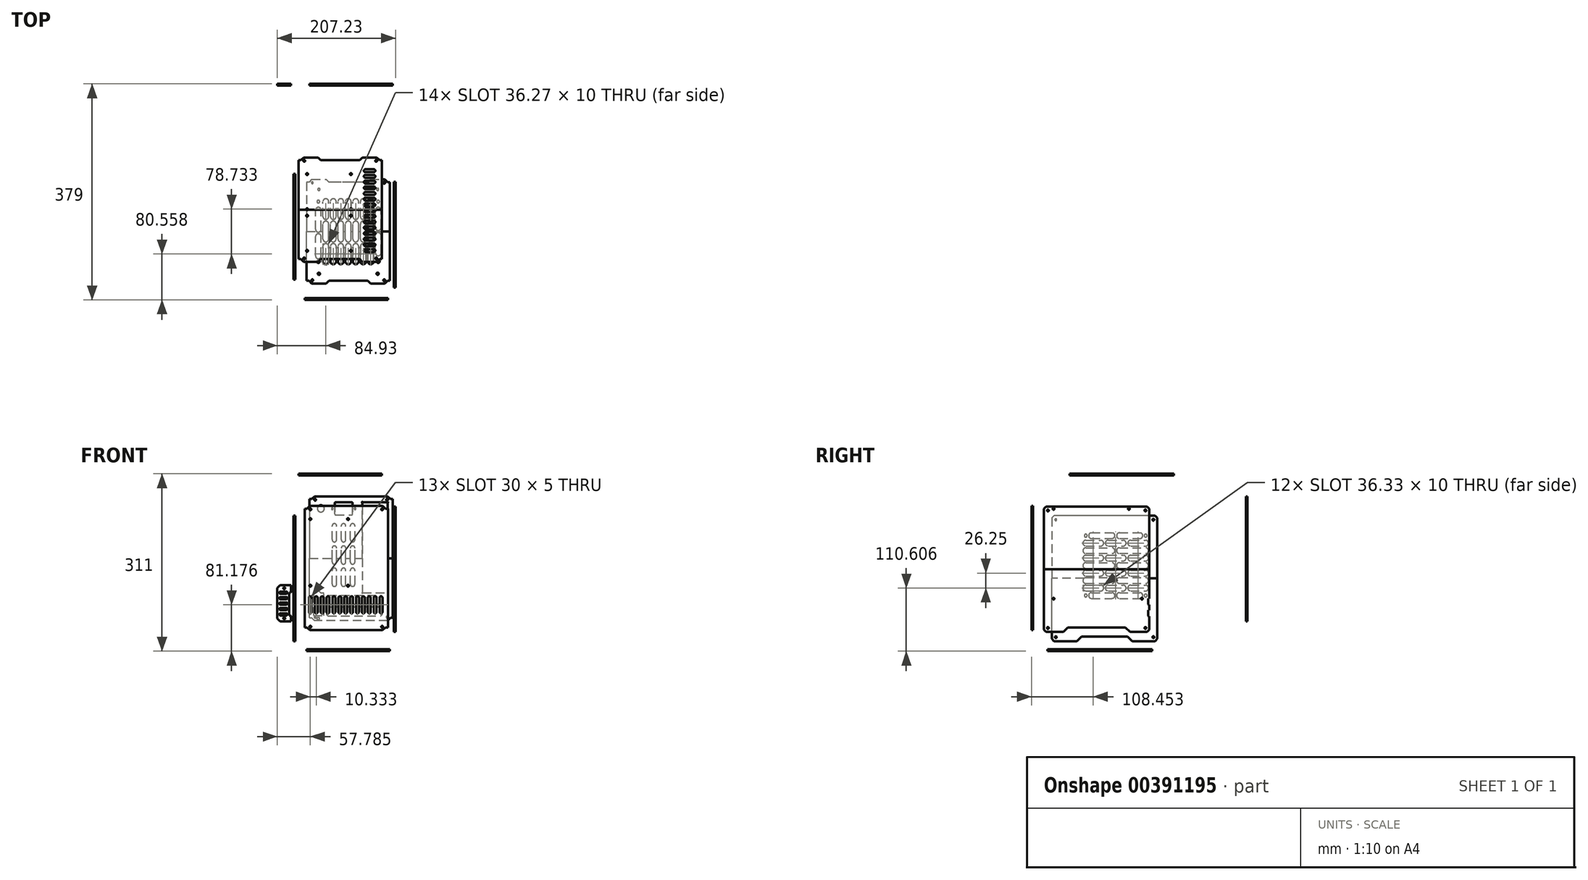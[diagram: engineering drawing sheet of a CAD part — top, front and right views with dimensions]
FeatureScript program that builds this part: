
annotation { "Feature Type Name" : "Feature", "Feature Type Description" : "" }
export const myFeature = defineFeature(function(context is Context, id is Id, definition is map)
    precondition{}
    {
        {
            var Q0;
            Q0=qCreatedBy(makeId("Front.planeOp"),FACE);
            var sketch = newSketch(context, id + "F0", { "sketchPlane" : qUnion([Q0])});
            skLineSegment(sketch, "E0.bottom", {"start": v(-76.44, 105.68) * mm, "end": v(69.56, 105.68) * mm});
            skLineSegment(sketch, "E0.top", {"start": v(-76.44, -7.32) * mm, "end": v(69.56, -7.32) * mm});
            skLineSegment(sketch, "E0.left", {"start": v(-76.44, 105.68) * mm, "end": v(-76.44, -7.32) * mm});
            skLineSegment(sketch, "E0.right", {"start": v(69.56, 105.68) * mm, "end": v(69.56, -7.32) * mm});
            skLineSegment(sketch, "E1", {"start": v(-76.44, 96.68) * mm, "end": v(-72.44, 96.68) * mm});
            skLineSegment(sketch, "E2", {"start": v(-72.44, 96.68) * mm, "end": v(-67.44, 101.68) * mm});
            skLineSegment(sketch, "E3", {"start": v(69.56, 96.68) * mm, "end": v(65.56, 96.68) * mm});
            skLineSegment(sketch, "E4", {"start": v(60.56, 101.68) * mm, "end": v(-67.44, 101.68) * mm});
            skLineSegment(sketch, "E5", {"start": v(60.56, 101.68) * mm, "end": v(65.56, 96.68) * mm});
            skLineSegment(sketch, "E6", {"start": v(-76.44, 95.68) * mm, "end": v(-66.44, 95.68) * mm, "construction": true});
            skCircle(sketch, "E7", {"center": v(-66.44, 95.68) * mm, "radius": 1.6 * mm});
            skLineSegment(sketch, "E8", {"start": v(69.56, 95.68) * mm, "end": v(59.56, 95.68) * mm, "construction": true});
            skCircle(sketch, "E9", {"center": v(59.56, 95.68) * mm, "radius": 1.6 * mm});
            skSolve(sketch);
        }
        {
            var Q0;
            {var subQ1=sQuery(id+"F0.wireOp",EDGE,"E0.top");Q0=makeQuery(id+"F0.imprint","IMPRINT",FACE,{"disambiguationData":[TD([[makeQuery(id+"F0.imprint","IMPRINT",EDGE,{"derivedFrom":subQ1}),1.0]])]});}
            extrude(context, id + "F1", {"entities" : qUnion([Q0]), "depth" : 3 * mm});
        }
        {
            var Q0;
            Q0=makeQuery(id+"F1.opExtrude","SWEPT_BODY",BODY,{"disambiguationData":[OSD([sQuery(id+"F0.wireOp",EDGE,"E0.bottom"),sQuery(id+"F0.wireOp",EDGE,"E0.top"),sQuery(id+"F0.wireOp",EDGE,"E0.left"),sQuery(id+"F0.wireOp",EDGE,"E0.right"),sQuery(id+"F0.wireOp",EDGE,"E1"),sQuery(id+"F0.wireOp",EDGE,"E2"),sQuery(id+"F0.wireOp",EDGE,"8kIEKiAh-QTEb-dtpp-JcTS-wpPMPQfBbqQd"),sQuery(id+"F0.wireOp",EDGE,"IAD0FTGy-GJaP-wMLm-guci-XfnhwucHu2uu"),sQuery(id+"F0.wireOp",EDGE,"IvHsRxJE-VIxi-RXbs-pRJC-tqeUj7lQNFDg"),sQuery(id+"F0.wireOp",EDGE,"jDx6nEBO-jJHg-Gf5S-wIms-nsZNRVFYcTxt")])]});
            var Q1;
            Q1=makeQuery(id+"F1.opExtrude","SWEPT_FACE",FACE,{"disambiguationData":[OSD([sQuery(id+"F0.wireOp",EDGE,"E0.top")])]});
            mirror(context, id + "F2", {"operationType" : NewBodyOperationType.ADD, "entities" : qUnion([Q0]), "mirrorPlane" : qUnion([Q1])});
        }
        {
            var Q0;
            {var subQ0=makeQuery(id+"F1.opExtrude","CAP_FACE",FACE,{"disambiguationData":[OSD([sQuery(id+"F0.wireOp",EDGE,"E0.bottom"),sQuery(id+"F0.wireOp",EDGE,"E0.top"),sQuery(id+"F0.wireOp",EDGE,"E0.left"),sQuery(id+"F0.wireOp",EDGE,"E0.right"),sQuery(id+"F0.wireOp",EDGE,"E1"),sQuery(id+"F0.wireOp",EDGE,"E2"),sQuery(id+"F0.wireOp",EDGE,"8kIEKiAh-QTEb-dtpp-JcTS-wpPMPQfBbqQd"),sQuery(id+"F0.wireOp",EDGE,"IAD0FTGy-GJaP-wMLm-guci-XfnhwucHu2uu"),sQuery(id+"F0.wireOp",EDGE,"IvHsRxJE-VIxi-RXbs-pRJC-tqeUj7lQNFDg"),sQuery(id+"F0.wireOp",EDGE,"jDx6nEBO-jJHg-Gf5S-wIms-nsZNRVFYcTxt")])],"isStart":false});Q0=makeQuery(id+"F2.boolean.opBoolean","MERGE",FACE,{"derivedFrom":[subQ0,makeQuery(id+"F2.opPattern","COPY",FACE,{"derivedFrom":subQ0,"instanceName":"1"})]});}
            var sketch = newSketch(context, id + "F3", { "sketchPlane" : qUnion([Q0])});
            skLineSegment(sketch, "E10", {"start": v(-66.44, -84.32) * mm, "end": v(-66.44, -116.32) * mm, "construction": true});
            skLineSegment(sketch, "E11.bottom", {"start": v(-66.44, 78.68) * mm, "end": v(-0.24, 78.68) * mm, "construction": true});
            skLineSegment(sketch, "E11.top", {"start": v(-66.44, -38.32) * mm, "end": v(-0.24, -38.32) * mm, "construction": true});
            skLineSegment(sketch, "E11.left", {"start": v(-66.44, 78.68) * mm, "end": v(-66.44, -38.32) * mm, "construction": true});
            skLineSegment(sketch, "E11.right", {"start": v(-0.24, 78.68) * mm, "end": v(-0.24, -38.32) * mm, "construction": true});
            skLineSegment(sketch, "E12", {"start": v(-66.44, 78.68) * mm, "end": v(-76.44, 78.68) * mm, "construction": true});
            skCircle(sketch, "E13", {"center": v(-0.24, 78.68) * mm, "radius": 1.6 * mm});
            skCircle(sketch, "E14", {"center": v(-66.44, 78.68) * mm, "radius": 1.6 * mm});
            skCircle(sketch, "E15", {"center": v(-66.44, -38.32) * mm, "radius": 1.6 * mm});
            skCircle(sketch, "E16", {"center": v(-0.24, -38.32) * mm, "radius": 1.6 * mm});
            skLineSegment(sketch, "E17", {"start": v(-66.44, -84.32) * mm, "end": v(-66.44, -59.32) * mm, "construction": true});
            skArc(sketch, "E18.0.startCap", {"start": v(-63.94, -84.32) * mm, "mid": v(-66.44, -86.82) * mm, "end": v(-68.94, -84.32) * mm});
            skArc(sketch, "E18.0.endCap", {"start": v(-68.94, -59.32) * mm, "mid": v(-66.44, -56.82) * mm, "end": v(-63.94, -59.32) * mm});
            skLineSegment(sketch, "E18.0.left", {"start": v(-68.94, -84.32) * mm, "end": v(-68.94, -59.32) * mm});
            skLineSegment(sketch, "E18.0.right", {"start": v(-63.94, -84.32) * mm, "end": v(-63.94, -59.32) * mm});
            skLineSegment(sketch, "E19.1.0.0", {"start": v(-56.11, -84.32) * mm, "end": v(-56.11, -59.32) * mm, "construction": true});
            skArc(sketch, "E19.1.0.1", {"start": v(-53.61, -84.32) * mm, "mid": v(-56.11, -86.82) * mm, "end": v(-58.61, -84.32) * mm});
            skArc(sketch, "E19.1.0.2", {"start": v(-58.61, -59.32) * mm, "mid": v(-56.11, -56.82) * mm, "end": v(-53.61, -59.32) * mm});
            skLineSegment(sketch, "E19.1.0.3", {"start": v(-53.61, -84.32) * mm, "end": v(-53.61, -59.32) * mm});
            skLineSegment(sketch, "E19.1.0.4", {"start": v(-58.61, -84.32) * mm, "end": v(-58.61, -59.32) * mm});
            skLineSegment(sketch, "E19.2.0.0", {"start": v(-45.78, -84.32) * mm, "end": v(-45.78, -59.32) * mm, "construction": true});
            skArc(sketch, "E19.2.0.1", {"start": v(-43.28, -84.32) * mm, "mid": v(-45.78, -86.82) * mm, "end": v(-48.28, -84.32) * mm});
            skArc(sketch, "E19.2.0.2", {"start": v(-48.28, -59.32) * mm, "mid": v(-45.78, -56.82) * mm, "end": v(-43.28, -59.32) * mm});
            skLineSegment(sketch, "E19.2.0.3", {"start": v(-43.28, -84.32) * mm, "end": v(-43.28, -59.32) * mm});
            skLineSegment(sketch, "E19.2.0.4", {"start": v(-48.28, -84.32) * mm, "end": v(-48.28, -59.32) * mm});
            skLineSegment(sketch, "E19.3.0.0", {"start": v(-35.45, -84.32) * mm, "end": v(-35.45, -59.32) * mm, "construction": true});
            skArc(sketch, "E19.3.0.1", {"start": v(-32.95, -84.32) * mm, "mid": v(-35.45, -86.82) * mm, "end": v(-37.95, -84.32) * mm});
            skArc(sketch, "E19.3.0.2", {"start": v(-37.95, -59.32) * mm, "mid": v(-35.45, -56.82) * mm, "end": v(-32.95, -59.32) * mm});
            skLineSegment(sketch, "E19.3.0.3", {"start": v(-32.95, -84.32) * mm, "end": v(-32.95, -59.32) * mm});
            skLineSegment(sketch, "E19.3.0.4", {"start": v(-37.95, -84.32) * mm, "end": v(-37.95, -59.32) * mm});
            skLineSegment(sketch, "E19.4.0.0", {"start": v(-25.11, -84.32) * mm, "end": v(-25.11, -59.32) * mm, "construction": true});
            skArc(sketch, "E19.4.0.1", {"start": v(-22.61, -84.32) * mm, "mid": v(-25.11, -86.82) * mm, "end": v(-27.61, -84.32) * mm});
            skArc(sketch, "E19.4.0.2", {"start": v(-27.61, -59.32) * mm, "mid": v(-25.11, -56.82) * mm, "end": v(-22.61, -59.32) * mm});
            skLineSegment(sketch, "E19.4.0.3", {"start": v(-22.61, -84.32) * mm, "end": v(-22.61, -59.32) * mm});
            skLineSegment(sketch, "E19.4.0.4", {"start": v(-27.61, -84.32) * mm, "end": v(-27.61, -59.32) * mm});
            skLineSegment(sketch, "E19.5.0.0", {"start": v(-14.78, -84.32) * mm, "end": v(-14.78, -59.32) * mm, "construction": true});
            skArc(sketch, "E19.5.0.1", {"start": v(-12.28, -84.32) * mm, "mid": v(-14.78, -86.82) * mm, "end": v(-17.28, -84.32) * mm});
            skArc(sketch, "E19.5.0.2", {"start": v(-17.28, -59.32) * mm, "mid": v(-14.78, -56.82) * mm, "end": v(-12.28, -59.32) * mm});
            skLineSegment(sketch, "E19.5.0.3", {"start": v(-12.28, -84.32) * mm, "end": v(-12.28, -59.32) * mm});
            skLineSegment(sketch, "E19.5.0.4", {"start": v(-17.28, -84.32) * mm, "end": v(-17.28, -59.32) * mm});
            skLineSegment(sketch, "E19.6.0.0", {"start": v(-4.45, -84.32) * mm, "end": v(-4.45, -59.32) * mm, "construction": true});
            skArc(sketch, "E19.6.0.1", {"start": v(-1.95, -84.32) * mm, "mid": v(-4.45, -86.82) * mm, "end": v(-6.95, -84.32) * mm});
            skArc(sketch, "E19.6.0.2", {"start": v(-6.95, -59.32) * mm, "mid": v(-4.45, -56.82) * mm, "end": v(-1.95, -59.32) * mm});
            skLineSegment(sketch, "E19.6.0.3", {"start": v(-1.95, -84.32) * mm, "end": v(-1.95, -59.32) * mm});
            skLineSegment(sketch, "E19.6.0.4", {"start": v(-6.95, -84.32) * mm, "end": v(-6.95, -59.32) * mm});
            skLineSegment(sketch, "E19.7.0.0", {"start": v(5.89, -84.32) * mm, "end": v(5.89, -59.32) * mm, "construction": true});
            skArc(sketch, "E19.7.0.1", {"start": v(8.39, -84.32) * mm, "mid": v(5.89, -86.82) * mm, "end": v(3.39, -84.32) * mm});
            skArc(sketch, "E19.7.0.2", {"start": v(3.39, -59.32) * mm, "mid": v(5.89, -56.82) * mm, "end": v(8.39, -59.32) * mm});
            skLineSegment(sketch, "E19.7.0.3", {"start": v(8.39, -84.32) * mm, "end": v(8.39, -59.32) * mm});
            skLineSegment(sketch, "E19.7.0.4", {"start": v(3.39, -84.32) * mm, "end": v(3.39, -59.32) * mm});
            skLineSegment(sketch, "E19.8.0.0", {"start": v(16.22, -84.32) * mm, "end": v(16.22, -59.32) * mm, "construction": true});
            skArc(sketch, "E19.8.0.1", {"start": v(18.72, -84.32) * mm, "mid": v(16.22, -86.82) * mm, "end": v(13.72, -84.32) * mm});
            skArc(sketch, "E19.8.0.2", {"start": v(13.72, -59.32) * mm, "mid": v(16.22, -56.82) * mm, "end": v(18.72, -59.32) * mm});
            skLineSegment(sketch, "E19.8.0.3", {"start": v(18.72, -84.32) * mm, "end": v(18.72, -59.32) * mm});
            skLineSegment(sketch, "E19.8.0.4", {"start": v(13.72, -84.32) * mm, "end": v(13.72, -59.32) * mm});
            skLineSegment(sketch, "E19.9.0.0", {"start": v(26.55, -84.32) * mm, "end": v(26.55, -59.32) * mm, "construction": true});
            skArc(sketch, "E19.9.0.1", {"start": v(29.05, -84.32) * mm, "mid": v(26.55, -86.82) * mm, "end": v(24.05, -84.32) * mm});
            skArc(sketch, "E19.9.0.2", {"start": v(24.05, -59.32) * mm, "mid": v(26.55, -56.82) * mm, "end": v(29.05, -59.32) * mm});
            skLineSegment(sketch, "E19.9.0.3", {"start": v(29.05, -84.32) * mm, "end": v(29.05, -59.32) * mm});
            skLineSegment(sketch, "E19.9.0.4", {"start": v(24.05, -84.32) * mm, "end": v(24.05, -59.32) * mm});
            skLineSegment(sketch, "E19.10.0.0", {"start": v(36.89, -84.32) * mm, "end": v(36.89, -59.32) * mm, "construction": true});
            skArc(sketch, "E19.10.0.1", {"start": v(39.39, -84.32) * mm, "mid": v(36.89, -86.82) * mm, "end": v(34.39, -84.32) * mm});
            skArc(sketch, "E19.10.0.2", {"start": v(34.39, -59.32) * mm, "mid": v(36.89, -56.82) * mm, "end": v(39.39, -59.32) * mm});
            skLineSegment(sketch, "E19.10.0.3", {"start": v(39.39, -84.32) * mm, "end": v(39.39, -59.32) * mm});
            skLineSegment(sketch, "E19.10.0.4", {"start": v(34.39, -84.32) * mm, "end": v(34.39, -59.32) * mm});
            skLineSegment(sketch, "E19.11.0.0", {"start": v(47.22, -84.32) * mm, "end": v(47.22, -59.32) * mm, "construction": true});
            skArc(sketch, "E19.11.0.1", {"start": v(49.72, -84.32) * mm, "mid": v(47.22, -86.82) * mm, "end": v(44.72, -84.32) * mm});
            skArc(sketch, "E19.11.0.2", {"start": v(44.72, -59.32) * mm, "mid": v(47.22, -56.82) * mm, "end": v(49.72, -59.32) * mm});
            skLineSegment(sketch, "E19.11.0.3", {"start": v(49.72, -84.32) * mm, "end": v(49.72, -59.32) * mm});
            skLineSegment(sketch, "E19.11.0.4", {"start": v(44.72, -84.32) * mm, "end": v(44.72, -59.32) * mm});
            skLineSegment(sketch, "E19.12.0.0", {"start": v(57.55, -84.32) * mm, "end": v(57.55, -59.32) * mm, "construction": true});
            skArc(sketch, "E19.12.0.1", {"start": v(60.05, -84.32) * mm, "mid": v(57.55, -86.82) * mm, "end": v(55.05, -84.32) * mm});
            skArc(sketch, "E19.12.0.2", {"start": v(55.05, -59.32) * mm, "mid": v(57.55, -56.82) * mm, "end": v(60.05, -59.32) * mm});
            skLineSegment(sketch, "E19.12.0.3", {"start": v(60.05, -84.32) * mm, "end": v(60.05, -59.32) * mm});
            skLineSegment(sketch, "E19.12.0.4", {"start": v(55.05, -84.32) * mm, "end": v(55.05, -59.32) * mm});
            skLineSegment(sketch, "E19.direction1", {"start": v(-68.94, -84.32) * mm, "end": v(-58.61, -84.32) * mm, "construction": true});
            skSolve(sketch);
        }
        {
            var Q0;
            Q0=qSketchRegion(id+"F3",true);
            extrude(context, id + "F4", {"entities" : qUnion([Q0]), "operationType" : NewBodyOperationType.REMOVE, "oppositeDirection" : true, "depth" : 3 * mm});
        }
        {
            var Q0;
            Q0=qCreatedBy(makeId("Right.planeOp"),FACE);
            cPlane(context, id + "F5", {"entities" : qUnion([Q0]), "cplaneType" : CPlaneType.OFFSET, "offset" : 80 * mm, "width" : 150 * mm, "height" : 150 * mm});
        }
        {
            var Q0;
            Q0=qCreatedBy(id+"F5.planeOp",FACE);
            var sketch = newSketch(context, id + "F6", { "sketchPlane" : qUnion([Q0])});
            skLineSegment(sketch, "E20.bottom", {"start": v(18.91, 100.63) * mm, "end": v(203.91, 100.63) * mm});
            skLineSegment(sketch, "E20.top", {"start": v(18.91, -9.37) * mm, "end": v(203.91, -9.37) * mm});
            skLineSegment(sketch, "E20.left", {"start": v(18.91, 100.63) * mm, "end": v(18.91, -9.37) * mm});
            skLineSegment(sketch, "E20.right", {"start": v(203.91, 100.63) * mm, "end": v(203.91, -9.37) * mm});
            skLineSegment(sketch, "E21", {"start": v(18.91, 96.63) * mm, "end": v(22.91, 100.63) * mm});
            skLineSegment(sketch, "E22", {"start": v(199.91, 100.63) * mm, "end": v(203.91, 96.63) * mm});
            skLineSegment(sketch, "E23", {"start": v(18.91, 93.63) * mm, "end": v(25.91, 93.63) * mm, "construction": true});
            skCircle(sketch, "E24", {"center": v(25.91, 93.63) * mm, "radius": 1.6 * mm});
            skLineSegment(sketch, "E25", {"start": v(203.91, 93.63) * mm, "end": v(196.91, 93.63) * mm, "construction": true});
            skCircle(sketch, "E26", {"center": v(196.91, 93.63) * mm, "radius": 1.6 * mm});
            skSolve(sketch);
        }
        {
            var Q0;
            {var subQ4=sQuery(id+"F6.wireOp",EDGE,"E20.top");Q0=makeQuery(id+"F6.imprint","IMPRINT",FACE,{"disambiguationData":[TD([[makeQuery(id+"F6.imprint","IMPRINT",EDGE,{"derivedFrom":subQ4}),1.0]])]});}
            extrude(context, id + "F7", {"entities" : qUnion([Q0]), "depth" : 3 * mm});
        }
        {
            var Q0;
            Q0=makeQuery(id+"F7.opExtrude","SWEPT_BODY",BODY,{"disambiguationData":[OSD([sQuery(id+"F6.wireOp",EDGE,"E20.bottom"),sQuery(id+"F6.wireOp",EDGE,"E20.top"),sQuery(id+"F6.wireOp",EDGE,"E20.left"),sQuery(id+"F6.wireOp",EDGE,"E20.right"),sQuery(id+"F6.wireOp",EDGE,"uhohLnhp-hqEh-HnCf-sw5P-UAyFwgDYjcBT"),sQuery(id+"F6.wireOp",EDGE,"PZ9vbapj-Vyhe-IVd5-wSIB-ihSb0FTefDFo"),sQuery(id+"F6.wireOp",EDGE,"Vy2RlQAS-aQ6k-OJzX-lqoE-WAFZ4NoHzz8E"),sQuery(id+"F6.wireOp",EDGE,"uOpGianr-bHoC-LPpd-ZrnQ-WT6fRq75YZDk"),sQuery(id+"F6.wireOp",EDGE,"ByD4MoDk-9vtG-w2Bj-nV2I-deXss6nWGu8L"),sQuery(id+"F6.wireOp",EDGE,"dErzSW6J-HGX5-GNXE-lozc-OmhnMsFbACEc"),sQuery(id+"F6.wireOp",EDGE,"oiYVu7ST-duG0-g5FE-uATR-zlAqLM0uh895"),sQuery(id+"F6.wireOp",EDGE,"fhnCciFL-T4Vn-rBCZ-nkKt-uSig2OXv9zq8")])]});
            var Q1;
            Q1=makeQuery(id+"F7.opExtrude","SWEPT_FACE",FACE,{"disambiguationData":[OSD([sQuery(id+"F6.wireOp",EDGE,"E20.top")])]});
            mirror(context, id + "F8", {"operationType" : NewBodyOperationType.ADD, "entities" : qUnion([Q0]), "mirrorPlane" : qUnion([Q1])});
        }
        {
            var Q0;
            {var subQ0=makeQuery(id+"F7.opExtrude","CAP_FACE",FACE,{"disambiguationData":[OSD([sQuery(id+"F6.wireOp",EDGE,"E20.bottom"),sQuery(id+"F6.wireOp",EDGE,"E20.top"),sQuery(id+"F6.wireOp",EDGE,"E20.left"),sQuery(id+"F6.wireOp",EDGE,"E20.right"),sQuery(id+"F6.wireOp",EDGE,"E21"),sQuery(id+"F6.wireOp",EDGE,"E22")])],"isStart":true});Q0=makeQuery(id+"F8.boolean.opBoolean","MERGE",FACE,{"derivedFrom":[subQ0,makeQuery(id+"F8.opPattern","COPY",FACE,{"derivedFrom":subQ0,"instanceName":"1"})]});}
            var sketch = newSketch(context, id + "F9", { "sketchPlane" : qUnion([Q0])});
            skLineSegment(sketch, "E27", {"start": v(-200.91, -67.37) * mm, "end": v(-200.91, 102.63) * mm, "construction": true});
            skLineSegment(sketch, "E28", {"start": v(-200.91, -67.37) * mm, "end": v(-30.91, -67.37) * mm, "construction": true});
            skLineSegment(sketch, "E29", {"start": v(-200.91, 102.63) * mm, "end": v(-30.91, 102.63) * mm, "construction": true});
            skLineSegment(sketch, "E30", {"start": v(-30.91, 102.63) * mm, "end": v(-30.91, -67.37) * mm, "construction": true});
            skLineSegment(sketch, "E31", {"start": v(-200.91, -60.97) * mm, "end": v(-190.71, -60.97) * mm, "construction": true});
            skCircle(sketch, "E32", {"center": v(-190.71, -60.97) * mm, "radius": 1.5 * mm});
            skLineSegment(sketch, "E33", {"start": v(-190.71, -60.97) * mm, "end": v(-35.81, -60.97) * mm, "construction": true});
            skCircle(sketch, "E34", {"center": v(-35.81, -60.97) * mm, "radius": 1.5 * mm});
            skLineSegment(sketch, "E35", {"start": v(-200.91, 96.43) * mm, "end": v(-167.91, 96.43) * mm, "construction": true});
            skCircle(sketch, "E36", {"center": v(-167.91, 96.43) * mm, "radius": 1.5 * mm});
            skLineSegment(sketch, "E37", {"start": v(-167.91, 96.43) * mm, "end": v(-35.81, 96.43) * mm, "construction": true});
            skCircle(sketch, "E38", {"center": v(-35.81, 96.43) * mm, "radius": 1.5 * mm});
            skLineSegment(sketch, "E39", {"start": v(-52.91, -119.37) * mm, "end": v(-60.91, -111.37) * mm});
            skLineSegment(sketch, "E40", {"start": v(-60.91, -111.37) * mm, "end": v(-161.91, -111.37) * mm});
            skLineSegment(sketch, "E41", {"start": v(-161.91, -111.37) * mm, "end": v(-169.91, -119.37) * mm});
            skLineSegment(sketch, "E42", {"start": v(-52.91, -119.37) * mm, "end": v(-169.91, -119.37) * mm});
            skLineSegment(sketch, "E43.bottom", {"start": v(-201.91, -60.57) * mm, "end": v(-203.91, -60.57) * mm});
            skLineSegment(sketch, "E43.top", {"start": v(-201.91, -71.57) * mm, "end": v(-203.91, -71.57) * mm});
            skLineSegment(sketch, "E43.left", {"start": v(-201.91, -60.57) * mm, "end": v(-201.91, -71.57) * mm});
            skLineSegment(sketch, "E43.right", {"start": v(-203.91, -60.57) * mm, "end": v(-203.91, -71.57) * mm});
            skLineSegment(sketch, "E44", {"start": v(-201.91, -66.07) * mm, "end": v(-200.91, -66.07) * mm, "construction": true});
            skLineSegment(sketch, "E45.bottom", {"start": v(-201.91, -80.87) * mm, "end": v(-203.91, -80.87) * mm});
            skLineSegment(sketch, "E45.top", {"start": v(-201.91, -91.87) * mm, "end": v(-203.91, -91.87) * mm});
            skLineSegment(sketch, "E45.left", {"start": v(-201.91, -80.87) * mm, "end": v(-201.91, -91.87) * mm});
            skLineSegment(sketch, "E45.right", {"start": v(-203.91, -80.87) * mm, "end": v(-203.91, -91.87) * mm});
            skLineSegment(sketch, "E46", {"start": v(-203.91, -80.87) * mm, "end": v(-203.91, -71.57) * mm, "construction": true});
            skLineSegment(sketch, "E47", {"start": v(-201.91, -71.57) * mm, "end": v(-201.91, -80.87) * mm, "construction": true});
            skLineSegment(sketch, "E48", {"start": v(-203.91, -86.37) * mm, "end": v(-207.88, -86.37) * mm, "construction": true});
            skLineSegment(sketch, "E49", {"start": v(-207.88, -86.37) * mm, "end": v(-207.88, -66.07) * mm, "construction": true});
            skPoint(sketch, "E49.endSnap0", {"position": v(-203.91, -66.07) * mm});
            skLineSegment(sketch, "E50", {"start": v(-207.88, -66.07) * mm, "end": v(-203.91, -66.07) * mm, "construction": true});
            skSolve(sketch);
        }
        {
            var Q0;
            Q0=qSketchRegion(id+"F9",true);
            var Q1;
            {var subQ0=sQuery(id+"F9.wireOp",EDGE,"b6TVsvgF-kPWZ-6Ni7-LZi2-MRGtpnM4VBQ9");Q1=makeQuery(id+"F9.imprint","IMPRINT",FACE,{"disambiguationData":[TD([[makeQuery(id+"F9.imprint","IMPRINT",EDGE,{"derivedFrom":subQ0}),-1.0]])]});}
            extrude(context, id + "F10", {"entities" : qUnion([Q0, Q1]), "operationType" : NewBodyOperationType.REMOVE, "oppositeDirection" : true, "depth" : 25 * mm});
        }
        {
            var Q0;
            Q0=qCreatedBy(makeId("Right.planeOp"),FACE);
            cPlane(context, id + "F11", {"entities" : qUnion([Q0]), "cplaneType" : CPlaneType.OFFSET, "offset" : 96 * mm, "oppositeDirection" : true, "width" : 150 * mm, "height" : 150 * mm});
        }
        {
            var Q0;
            Q0=qCreatedBy(id+"F11.planeOp",FACE);
            var sketch = newSketch(context, id + "F12", { "sketchPlane" : qUnion([Q0])});
            skLineSegment(sketch, "E51.bottom", {"start": v(217.79, 84.48) * mm, "end": v(32.79, 84.48) * mm});
            skLineSegment(sketch, "E51.top", {"start": v(217.79, -25.52) * mm, "end": v(32.79, -25.52) * mm});
            skLineSegment(sketch, "E51.left", {"start": v(217.79, 84.48) * mm, "end": v(217.79, -25.52) * mm});
            skLineSegment(sketch, "E51.right", {"start": v(32.79, 84.48) * mm, "end": v(32.79, -25.52) * mm});
            skLineSegment(sketch, "E52", {"start": v(217.79, 80.48) * mm, "end": v(213.79, 84.48) * mm});
            skLineSegment(sketch, "E53", {"start": v(36.79, 84.48) * mm, "end": v(32.79, 80.48) * mm});
            skLineSegment(sketch, "E54", {"start": v(217.79, 77.48) * mm, "end": v(210.79, 77.48) * mm, "construction": true});
            skCircle(sketch, "E55", {"center": v(210.79, 77.48) * mm, "radius": 1.6 * mm});
            skLineSegment(sketch, "E56", {"start": v(32.79, 77.48) * mm, "end": v(39.79, 77.48) * mm, "construction": true});
            skCircle(sketch, "E57", {"center": v(39.79, 77.48) * mm, "radius": 1.6 * mm});
            skSolve(sketch);
        }
        {
            var Q0;
            {var subQ1=sQuery(id+"F12.wireOp",EDGE,"E51.top");Q0=makeQuery(id+"F12.imprint","IMPRINT",FACE,{"disambiguationData":[TD([[makeQuery(id+"F12.imprint","IMPRINT",EDGE,{"derivedFrom":subQ1}),-1.0]])]});}
            extrude(context, id + "F13", {"entities" : qUnion([Q0]), "depth" : 3 * mm});
        }
        {
            var Q0;
            Q0=makeQuery(id+"F13.opExtrude","SWEPT_BODY",BODY,{"disambiguationData":[OSD([sQuery(id+"F12.wireOp",EDGE,"E51.bottom"),sQuery(id+"F12.wireOp",EDGE,"E51.top"),sQuery(id+"F12.wireOp",EDGE,"E51.left"),sQuery(id+"F12.wireOp",EDGE,"E51.right"),sQuery(id+"F12.wireOp",EDGE,"E52"),sQuery(id+"F12.wireOp",EDGE,"E53")])]});
            var Q1;
            Q1=makeQuery(id+"F13.opExtrude","SWEPT_FACE",FACE,{"disambiguationData":[OSD([sQuery(id+"F12.wireOp",EDGE,"E51.top")])]});
            mirror(context, id + "F14", {"operationType" : NewBodyOperationType.ADD, "entities" : qUnion([Q0]), "mirrorPlane" : qUnion([Q1])});
        }
        {
            var Q0;
            {var subQ0=makeQuery(id+"F13.opExtrude","CAP_FACE",FACE,{"disambiguationData":[OSD([sQuery(id+"F12.wireOp",EDGE,"E51.bottom"),sQuery(id+"F12.wireOp",EDGE,"E51.top"),sQuery(id+"F12.wireOp",EDGE,"E51.left"),sQuery(id+"F12.wireOp",EDGE,"E51.right"),sQuery(id+"F12.wireOp",EDGE,"E52"),sQuery(id+"F12.wireOp",EDGE,"E53")])],"isStart":true});Q0=makeQuery(id+"F14.boolean.opBoolean","MERGE",FACE,{"derivedFrom":[subQ0,makeQuery(id+"F14.opPattern","COPY",FACE,{"derivedFrom":subQ0,"instanceName":"1"})]});}
            var sketch = newSketch(context, id + "F15", { "sketchPlane" : qUnion([Q0])});
            skLineSegment(sketch, "E58", {"start": v(-217.79, 54.48) * mm, "end": v(-197.29, 54.48) * mm, "construction": true});
            skLineSegment(sketch, "E59", {"start": v(-197.29, 54.48) * mm, "end": v(-197.29, -60.52) * mm, "construction": true});
            skLineSegment(sketch, "E60", {"start": v(-197.29, 49.48) * mm, "end": v(-187.29, 49.48) * mm, "construction": true});
            skLineSegment(sketch, "E61", {"start": v(-187.29, 49.48) * mm, "end": v(-151.29, 49.48) * mm, "construction": true});
            skLineSegment(sketch, "E62", {"start": v(-197.29, 36.36) * mm, "end": v(-170.95, 36.36) * mm, "construction": true});
            skLineSegment(sketch, "E63", {"start": v(-197.29, 23.23) * mm, "end": v(-151.29, 23.23) * mm, "construction": true});
            skLineSegment(sketch, "E64", {"start": v(-197.29, 10.1) * mm, "end": v(-170.95, 10.1) * mm, "construction": true});
            skLineSegment(sketch, "E65", {"start": v(-197.29, -3.02) * mm, "end": v(-151.29, -3.02) * mm, "construction": true});
            skLineSegment(sketch, "E66", {"start": v(-197.29, -16.14) * mm, "end": v(-170.95, -16.14) * mm, "construction": true});
            skLineSegment(sketch, "E67", {"start": v(-197.29, -29.27) * mm, "end": v(-151.29, -29.27) * mm, "construction": true});
            skLineSegment(sketch, "E68", {"start": v(-197.29, -42.4) * mm, "end": v(-170.95, -42.4) * mm, "construction": true});
            skLineSegment(sketch, "E69", {"start": v(-197.29, -55.52) * mm, "end": v(-187.29, -55.52) * mm, "construction": true});
            skLineSegment(sketch, "E70", {"start": v(-187.29, -55.52) * mm, "end": v(-151.29, -55.52) * mm, "construction": true});
            skCircle(sketch, "E71", {"center": v(-197.29, 49.48) * mm, "radius": 2.55 * mm});
            skLineSegment(sketch, "E72", {"start": v(-102.29, 49.48) * mm, "end": v(-92.29, 49.48) * mm, "construction": true});
            skPoint(sketch, "E72.endSnap0", {"position": v(-82.69, 49.48) * mm});
            skCircle(sketch, "E73", {"center": v(-92.29, 49.48) * mm, "radius": 2.55 * mm});
            skLineSegment(sketch, "E74", {"start": v(-151.29, 49.48) * mm, "end": v(-138.29, 49.48) * mm, "construction": true});
            skLineSegment(sketch, "E75", {"start": v(-138.29, 49.48) * mm, "end": v(-102.29, 49.48) * mm, "construction": true});
            skArc(sketch, "E76.0.startCap", {"start": v(-187.29, 44.48) * mm, "mid": v(-192.29, 49.48) * mm, "end": v(-187.29, 54.48) * mm});
            skArc(sketch, "E76.0.endCap", {"start": v(-151.29, 54.48) * mm, "mid": v(-146.29, 49.48) * mm, "end": v(-151.29, 44.48) * mm});
            skLineSegment(sketch, "E76.0.left", {"start": v(-187.29, 54.48) * mm, "end": v(-151.29, 54.48) * mm});
            skLineSegment(sketch, "E76.0.right", {"start": v(-187.29, 44.48) * mm, "end": v(-151.29, 44.48) * mm});
            skArc(sketch, "E76.1.startCap", {"start": v(-138.29, 44.48) * mm, "mid": v(-143.29, 49.48) * mm, "end": v(-138.29, 54.48) * mm});
            skArc(sketch, "E76.1.endCap", {"start": v(-102.29, 54.48) * mm, "mid": v(-97.29, 49.48) * mm, "end": v(-102.29, 44.48) * mm});
            skLineSegment(sketch, "E76.1.left", {"start": v(-138.29, 54.48) * mm, "end": v(-102.29, 54.48) * mm});
            skLineSegment(sketch, "E76.1.right", {"start": v(-138.29, 44.48) * mm, "end": v(-102.29, 44.48) * mm});
            skLineSegment(sketch, "E77", {"start": v(-170.95, 36.36) * mm, "end": v(-157.95, 36.36) * mm, "construction": true});
            skLineSegment(sketch, "E78", {"start": v(-157.95, 36.36) * mm, "end": v(-131.62, 36.36) * mm, "construction": true});
            skLineSegment(sketch, "E79", {"start": v(-131.62, 36.36) * mm, "end": v(-118.62, 36.36) * mm, "construction": true});
            skLineSegment(sketch, "E80", {"start": v(-118.62, 36.36) * mm, "end": v(-92.29, 36.36) * mm, "construction": true});
            skArc(sketch, "E81.0.startCap", {"start": v(-197.29, 31.36) * mm, "mid": v(-202.29, 36.36) * mm, "end": v(-197.29, 41.36) * mm});
            skArc(sketch, "E81.0.endCap", {"start": v(-170.95, 41.36) * mm, "mid": v(-165.95, 36.36) * mm, "end": v(-170.95, 31.36) * mm});
            skLineSegment(sketch, "E81.0.left", {"start": v(-197.29, 41.36) * mm, "end": v(-170.95, 41.36) * mm});
            skLineSegment(sketch, "E81.0.right", {"start": v(-197.29, 31.36) * mm, "end": v(-170.95, 31.36) * mm});
            skArc(sketch, "E81.1.startCap", {"start": v(-157.95, 31.36) * mm, "mid": v(-162.95, 36.36) * mm, "end": v(-157.95, 41.36) * mm});
            skArc(sketch, "E81.1.endCap", {"start": v(-131.62, 41.36) * mm, "mid": v(-126.62, 36.36) * mm, "end": v(-131.62, 31.36) * mm});
            skLineSegment(sketch, "E81.1.left", {"start": v(-157.95, 41.36) * mm, "end": v(-131.62, 41.36) * mm});
            skLineSegment(sketch, "E81.1.right", {"start": v(-157.95, 31.36) * mm, "end": v(-131.62, 31.36) * mm});
            skArc(sketch, "E81.2.startCap", {"start": v(-118.62, 31.36) * mm, "mid": v(-123.62, 36.36) * mm, "end": v(-118.62, 41.36) * mm});
            skArc(sketch, "E81.2.endCap", {"start": v(-92.29, 41.36) * mm, "mid": v(-87.29, 36.36) * mm, "end": v(-92.29, 31.36) * mm});
            skLineSegment(sketch, "E81.2.left", {"start": v(-118.62, 41.36) * mm, "end": v(-92.29, 41.36) * mm});
            skLineSegment(sketch, "E81.2.right", {"start": v(-118.62, 31.36) * mm, "end": v(-92.29, 31.36) * mm});
            skLineSegment(sketch, "E82", {"start": v(-151.29, 23.23) * mm, "end": v(-138.29, 23.23) * mm, "construction": true});
            skLineSegment(sketch, "E83", {"start": v(-138.29, 23.23) * mm, "end": v(-92.29, 23.23) * mm, "construction": true});
            skArc(sketch, "E84.0.startCap", {"start": v(-197.29, 18.23) * mm, "mid": v(-202.29, 23.23) * mm, "end": v(-197.29, 28.23) * mm});
            skArc(sketch, "E84.0.endCap", {"start": v(-151.29, 28.23) * mm, "mid": v(-146.29, 23.23) * mm, "end": v(-151.29, 18.23) * mm});
            skLineSegment(sketch, "E84.0.left", {"start": v(-197.29, 28.23) * mm, "end": v(-151.29, 28.23) * mm});
            skLineSegment(sketch, "E84.0.right", {"start": v(-197.29, 18.23) * mm, "end": v(-151.29, 18.23) * mm});
            skArc(sketch, "E84.1.startCap", {"start": v(-138.29, 18.23) * mm, "mid": v(-143.29, 23.23) * mm, "end": v(-138.29, 28.23) * mm});
            skArc(sketch, "E84.1.endCap", {"start": v(-92.29, 28.23) * mm, "mid": v(-87.29, 23.23) * mm, "end": v(-92.29, 18.23) * mm});
            skLineSegment(sketch, "E84.1.left", {"start": v(-138.29, 28.23) * mm, "end": v(-92.29, 28.23) * mm});
            skLineSegment(sketch, "E84.1.right", {"start": v(-138.29, 18.23) * mm, "end": v(-92.29, 18.23) * mm});
            skLineSegment(sketch, "E85", {"start": v(-170.95, 10.1) * mm, "end": v(-157.95, 10.1) * mm, "construction": true});
            skLineSegment(sketch, "E86", {"start": v(-157.95, 10.1) * mm, "end": v(-131.62, 10.1) * mm, "construction": true});
            skLineSegment(sketch, "E87", {"start": v(-131.62, 10.1) * mm, "end": v(-118.62, 10.1) * mm, "construction": true});
            skLineSegment(sketch, "E88", {"start": v(-118.62, 10.1) * mm, "end": v(-92.29, 10.1) * mm, "construction": true});
            skArc(sketch, "E89.0.startCap", {"start": v(-197.29, 5.1) * mm, "mid": v(-202.29, 10.1) * mm, "end": v(-197.29, 15.1) * mm});
            skArc(sketch, "E89.0.endCap", {"start": v(-170.95, 15.1) * mm, "mid": v(-165.95, 10.1) * mm, "end": v(-170.95, 5.1) * mm});
            skLineSegment(sketch, "E89.0.left", {"start": v(-197.29, 15.1) * mm, "end": v(-170.95, 15.1) * mm});
            skLineSegment(sketch, "E89.0.right", {"start": v(-197.29, 5.1) * mm, "end": v(-170.95, 5.1) * mm});
            skArc(sketch, "E89.1.startCap", {"start": v(-157.95, 5.1) * mm, "mid": v(-162.95, 10.1) * mm, "end": v(-157.95, 15.1) * mm});
            skArc(sketch, "E89.1.endCap", {"start": v(-131.62, 15.1) * mm, "mid": v(-126.62, 10.1) * mm, "end": v(-131.62, 5.1) * mm});
            skLineSegment(sketch, "E89.1.left", {"start": v(-157.95, 15.1) * mm, "end": v(-131.62, 15.1) * mm});
            skLineSegment(sketch, "E89.1.right", {"start": v(-157.95, 5.1) * mm, "end": v(-131.62, 5.1) * mm});
            skArc(sketch, "E89.2.startCap", {"start": v(-118.62, 5.1) * mm, "mid": v(-123.62, 10.1) * mm, "end": v(-118.62, 15.1) * mm});
            skArc(sketch, "E89.2.endCap", {"start": v(-92.29, 15.1) * mm, "mid": v(-87.29, 10.1) * mm, "end": v(-92.29, 5.1) * mm});
            skLineSegment(sketch, "E89.2.left", {"start": v(-118.62, 15.1) * mm, "end": v(-92.29, 15.1) * mm});
            skLineSegment(sketch, "E89.2.right", {"start": v(-118.62, 5.1) * mm, "end": v(-92.29, 5.1) * mm});
            skLineSegment(sketch, "E90", {"start": v(-151.29, -3.02) * mm, "end": v(-138.29, -3.02) * mm, "construction": true});
            skLineSegment(sketch, "E91", {"start": v(-138.29, -3.02) * mm, "end": v(-92.29, -3.02) * mm, "construction": true});
            skLineSegment(sketch, "E92", {"start": v(-170.95, -16.14) * mm, "end": v(-157.95, -16.14) * mm, "construction": true});
            skLineSegment(sketch, "E93", {"start": v(-157.95, -16.14) * mm, "end": v(-131.62, -16.14) * mm, "construction": true});
            skLineSegment(sketch, "E94", {"start": v(-131.62, -16.14) * mm, "end": v(-118.62, -16.14) * mm, "construction": true});
            skLineSegment(sketch, "E95", {"start": v(-118.62, -16.14) * mm, "end": v(-92.29, -16.14) * mm, "construction": true});
            skLineSegment(sketch, "E96", {"start": v(-151.29, -29.27) * mm, "end": v(-138.29, -29.27) * mm, "construction": true});
            skLineSegment(sketch, "E97", {"start": v(-138.29, -29.27) * mm, "end": v(-92.29, -29.27) * mm, "construction": true});
            skLineSegment(sketch, "E98", {"start": v(-170.95, -42.4) * mm, "end": v(-157.95, -42.4) * mm, "construction": true});
            skLineSegment(sketch, "E99", {"start": v(-157.95, -42.4) * mm, "end": v(-131.62, -42.4) * mm, "construction": true});
            skLineSegment(sketch, "E100", {"start": v(-131.62, -42.4) * mm, "end": v(-118.62, -42.4) * mm, "construction": true});
            skLineSegment(sketch, "E101", {"start": v(-118.62, -42.4) * mm, "end": v(-92.29, -42.4) * mm, "construction": true});
            skLineSegment(sketch, "E102", {"start": v(-151.29, -55.52) * mm, "end": v(-138.29, -55.52) * mm, "construction": true});
            skLineSegment(sketch, "E103", {"start": v(-138.29, -55.52) * mm, "end": v(-102.29, -55.52) * mm, "construction": true});
            skLineSegment(sketch, "E104", {"start": v(-102.29, -55.52) * mm, "end": v(-92.29, -55.52) * mm, "construction": true});
            skArc(sketch, "E105.0.startCap", {"start": v(-197.29, -8.02) * mm, "mid": v(-202.29, -3.02) * mm, "end": v(-197.29, 1.98) * mm});
            skArc(sketch, "E105.0.endCap", {"start": v(-151.29, 1.98) * mm, "mid": v(-146.29, -3.02) * mm, "end": v(-151.29, -8.02) * mm});
            skLineSegment(sketch, "E105.0.left", {"start": v(-197.29, 1.98) * mm, "end": v(-151.29, 1.98) * mm});
            skLineSegment(sketch, "E105.0.right", {"start": v(-197.29, -8.02) * mm, "end": v(-151.29, -8.02) * mm});
            skArc(sketch, "E105.1.startCap", {"start": v(-138.29, -8.02) * mm, "mid": v(-143.29, -3.02) * mm, "end": v(-138.29, 1.98) * mm});
            skArc(sketch, "E105.1.endCap", {"start": v(-92.29, 1.98) * mm, "mid": v(-87.29, -3.02) * mm, "end": v(-92.29, -8.02) * mm});
            skLineSegment(sketch, "E105.1.left", {"start": v(-138.29, 1.98) * mm, "end": v(-92.29, 1.98) * mm});
            skLineSegment(sketch, "E105.1.right", {"start": v(-138.29, -8.02) * mm, "end": v(-92.29, -8.02) * mm});
            skArc(sketch, "E105.2.startCap", {"start": v(-197.29, -21.14) * mm, "mid": v(-202.29, -16.14) * mm, "end": v(-197.29, -11.14) * mm});
            skArc(sketch, "E105.2.endCap", {"start": v(-170.95, -11.14) * mm, "mid": v(-165.95, -16.14) * mm, "end": v(-170.95, -21.14) * mm});
            skLineSegment(sketch, "E105.2.left", {"start": v(-197.29, -11.14) * mm, "end": v(-170.95, -11.14) * mm});
            skLineSegment(sketch, "E105.2.right", {"start": v(-197.29, -21.14) * mm, "end": v(-170.95, -21.14) * mm});
            skArc(sketch, "E105.3.startCap", {"start": v(-157.95, -21.14) * mm, "mid": v(-162.95, -16.14) * mm, "end": v(-157.95, -11.14) * mm});
            skArc(sketch, "E105.3.endCap", {"start": v(-131.62, -11.14) * mm, "mid": v(-126.62, -16.14) * mm, "end": v(-131.62, -21.14) * mm});
            skLineSegment(sketch, "E105.3.left", {"start": v(-157.95, -11.14) * mm, "end": v(-131.62, -11.14) * mm});
            skLineSegment(sketch, "E105.3.right", {"start": v(-157.95, -21.14) * mm, "end": v(-131.62, -21.14) * mm});
            skArc(sketch, "E105.4.startCap", {"start": v(-118.62, -21.14) * mm, "mid": v(-123.62, -16.14) * mm, "end": v(-118.62, -11.14) * mm});
            skArc(sketch, "E105.4.endCap", {"start": v(-92.29, -11.14) * mm, "mid": v(-87.29, -16.14) * mm, "end": v(-92.29, -21.14) * mm});
            skLineSegment(sketch, "E105.4.left", {"start": v(-118.62, -11.14) * mm, "end": v(-92.29, -11.14) * mm});
            skLineSegment(sketch, "E105.4.right", {"start": v(-118.62, -21.14) * mm, "end": v(-92.29, -21.14) * mm});
            skArc(sketch, "E106.0.startCap", {"start": v(-197.29, -34.27) * mm, "mid": v(-202.29, -29.27) * mm, "end": v(-197.29, -24.27) * mm});
            skArc(sketch, "E106.0.endCap", {"start": v(-151.29, -24.27) * mm, "mid": v(-146.29, -29.27) * mm, "end": v(-151.29, -34.27) * mm});
            skLineSegment(sketch, "E106.0.left", {"start": v(-197.29, -24.27) * mm, "end": v(-151.29, -24.27) * mm});
            skLineSegment(sketch, "E106.0.right", {"start": v(-197.29, -34.27) * mm, "end": v(-151.29, -34.27) * mm});
            skArc(sketch, "E106.1.startCap", {"start": v(-138.29, -34.27) * mm, "mid": v(-143.29, -29.27) * mm, "end": v(-138.29, -24.27) * mm});
            skArc(sketch, "E106.1.endCap", {"start": v(-92.29, -24.27) * mm, "mid": v(-87.29, -29.27) * mm, "end": v(-92.29, -34.27) * mm});
            skLineSegment(sketch, "E106.1.left", {"start": v(-138.29, -24.27) * mm, "end": v(-92.29, -24.27) * mm});
            skLineSegment(sketch, "E106.1.right", {"start": v(-138.29, -34.27) * mm, "end": v(-92.29, -34.27) * mm});
            skArc(sketch, "E106.2.startCap", {"start": v(-197.29, -47.4) * mm, "mid": v(-202.29, -42.4) * mm, "end": v(-197.29, -37.4) * mm});
            skArc(sketch, "E106.2.endCap", {"start": v(-170.95, -37.4) * mm, "mid": v(-165.95, -42.4) * mm, "end": v(-170.95, -47.4) * mm});
            skLineSegment(sketch, "E106.2.left", {"start": v(-197.29, -37.4) * mm, "end": v(-170.95, -37.4) * mm});
            skLineSegment(sketch, "E106.2.right", {"start": v(-197.29, -47.4) * mm, "end": v(-170.95, -47.4) * mm});
            skArc(sketch, "E106.3.startCap", {"start": v(-157.95, -47.4) * mm, "mid": v(-162.95, -42.4) * mm, "end": v(-157.95, -37.4) * mm});
            skArc(sketch, "E106.3.endCap", {"start": v(-131.62, -37.4) * mm, "mid": v(-126.62, -42.4) * mm, "end": v(-131.62, -47.4) * mm});
            skLineSegment(sketch, "E106.3.left", {"start": v(-157.95, -37.4) * mm, "end": v(-131.62, -37.4) * mm});
            skLineSegment(sketch, "E106.3.right", {"start": v(-157.95, -47.4) * mm, "end": v(-131.62, -47.4) * mm});
            skArc(sketch, "E106.4.startCap", {"start": v(-118.62, -47.4) * mm, "mid": v(-123.62, -42.4) * mm, "end": v(-118.62, -37.4) * mm});
            skArc(sketch, "E106.4.endCap", {"start": v(-92.29, -37.4) * mm, "mid": v(-87.29, -42.4) * mm, "end": v(-92.29, -47.4) * mm});
            skLineSegment(sketch, "E106.4.left", {"start": v(-118.62, -37.4) * mm, "end": v(-92.29, -37.4) * mm});
            skLineSegment(sketch, "E106.4.right", {"start": v(-118.62, -47.4) * mm, "end": v(-92.29, -47.4) * mm});
            skArc(sketch, "E106.5.startCap", {"start": v(-187.29, -60.52) * mm, "mid": v(-192.29, -55.52) * mm, "end": v(-187.29, -50.52) * mm});
            skArc(sketch, "E106.5.endCap", {"start": v(-151.29, -50.52) * mm, "mid": v(-146.29, -55.52) * mm, "end": v(-151.29, -60.52) * mm});
            skLineSegment(sketch, "E106.5.left", {"start": v(-187.29, -50.52) * mm, "end": v(-151.29, -50.52) * mm});
            skLineSegment(sketch, "E106.5.right", {"start": v(-187.29, -60.52) * mm, "end": v(-151.29, -60.52) * mm});
            skArc(sketch, "E106.6.startCap", {"start": v(-138.29, -60.52) * mm, "mid": v(-143.29, -55.52) * mm, "end": v(-138.29, -50.52) * mm});
            skArc(sketch, "E106.6.endCap", {"start": v(-102.29, -50.52) * mm, "mid": v(-97.29, -55.52) * mm, "end": v(-102.29, -60.52) * mm});
            skLineSegment(sketch, "E106.6.left", {"start": v(-138.29, -50.52) * mm, "end": v(-102.29, -50.52) * mm});
            skLineSegment(sketch, "E106.6.right", {"start": v(-138.29, -60.52) * mm, "end": v(-102.29, -60.52) * mm});
            skCircle(sketch, "E107", {"center": v(-197.29, -55.52) * mm, "radius": 2.55 * mm});
            skCircle(sketch, "E108", {"center": v(-92.29, -55.52) * mm, "radius": 2.55 * mm});
            skLineSegment(sketch, "E109", {"start": v(-173.79, -135.52) * mm, "end": v(-165.79, -127.52) * mm});
            skLineSegment(sketch, "E110", {"start": v(-165.79, -127.52) * mm, "end": v(-84.79, -127.52) * mm});
            skLineSegment(sketch, "E111", {"start": v(-84.79, -127.52) * mm, "end": v(-76.79, -135.52) * mm});
            skLineSegment(sketch, "E112", {"start": v(-76.79, -135.52) * mm, "end": v(-173.79, -135.52) * mm});
            skSolve(sketch);
        }
        {
            var Q0;
            Q0=qSketchRegion(id+"F15",true);
            var Q1;
            {var subQ0=sQuery(id+"F15.wireOp",EDGE,"eD3hBwOG-1YSv-rIqv-KxOD-YYoGhDVYBiqk");Q1=makeQuery(id+"F15.imprint","IMPRINT",FACE,{"disambiguationData":[TD([[makeQuery(id+"F15.imprint","IMPRINT",EDGE,{"derivedFrom":subQ0}),-1.0]])]});}
            extrude(context, id + "F16", {"entities" : qUnion([Q0, Q1]), "operationType" : NewBodyOperationType.REMOVE, "oppositeDirection" : true, "depth" : 25 * mm});
        }
        {
            var Q0;
            Q0=qCreatedBy(makeId("Top.planeOp"),FACE);
            cPlane(context, id + "F17", {"entities" : qUnion([Q0]), "cplaneType" : CPlaneType.OFFSET, "offset" : 155 * mm, "width" : 150 * mm, "height" : 150 * mm});
        }
        {
            var Q0;
            Q0=qCreatedBy(id+"F17.planeOp",FACE);
            var sketch = newSketch(context, id + "F18", { "sketchPlane" : qUnion([Q0])});
            skLineSegment(sketch, "E113.bottom", {"start": v(-87.02, 155.37) * mm, "end": v(58.98, 155.37) * mm});
            skLineSegment(sketch, "E113.top", {"start": v(-87.02, 63.87) * mm, "end": v(58.98, 63.87) * mm});
            skLineSegment(sketch, "E113.left", {"start": v(-87.02, 155.37) * mm, "end": v(-87.02, 63.87) * mm});
            skLineSegment(sketch, "E113.right", {"start": v(58.98, 155.37) * mm, "end": v(58.98, 63.87) * mm});
            skLineSegment(sketch, "E114", {"start": v(-78.02, 63.87) * mm, "end": v(-83.02, 68.87) * mm});
            skLineSegment(sketch, "E115", {"start": v(49.98, 63.87) * mm, "end": v(54.98, 68.87) * mm});
            skLineSegment(sketch, "E116", {"start": v(-83.02, 68.87) * mm, "end": v(-87.02, 68.87) * mm});
            skLineSegment(sketch, "E117", {"start": v(54.98, 68.87) * mm, "end": v(58.98, 68.87) * mm});
            skLineSegment(sketch, "E118", {"start": v(48.98, 63.87) * mm, "end": v(48.98, 69.87) * mm, "construction": true});
            skCircle(sketch, "E119", {"center": v(48.98, 69.87) * mm, "radius": 1.6 * mm});
            skLineSegment(sketch, "E120", {"start": v(-77.02, 63.87) * mm, "end": v(-77.02, 69.87) * mm, "construction": true});
            skCircle(sketch, "E121", {"center": v(-77.02, 69.87) * mm, "radius": 1.6 * mm});
            skLineSegment(sketch, "E122", {"start": v(-53.02, 63.87) * mm, "end": v(-48.02, 68.87) * mm});
            skLineSegment(sketch, "E123", {"start": v(-48.02, 68.87) * mm, "end": v(19.98, 68.87) * mm});
            skLineSegment(sketch, "E124", {"start": v(19.98, 68.87) * mm, "end": v(24.98, 63.87) * mm});
            skSolve(sketch);
        }
        {
            var Q0;
            {var subQ1=sQuery(id+"F18.wireOp",EDGE,"E113.bottom");Q0=makeQuery(id+"F18.imprint","IMPRINT",FACE,{"disambiguationData":[TD([[makeQuery(id+"F18.imprint","IMPRINT",EDGE,{"derivedFrom":subQ1}),-1.0]])]});}
            extrude(context, id + "F19", {"entities" : qUnion([Q0]), "depth" : 3 * mm});
        }
        {
            var Q0;
            Q0=makeQuery(id+"F19.opExtrude","SWEPT_BODY",BODY,{"disambiguationData":[OSD([sQuery(id+"F18.wireOp",EDGE,"E113.bottom"),sQuery(id+"F18.wireOp",EDGE,"E113.top"),sQuery(id+"F18.wireOp",EDGE,"E113.left"),sQuery(id+"F18.wireOp",EDGE,"E113.right"),sQuery(id+"F18.wireOp",EDGE,"E114"),sQuery(id+"F18.wireOp",EDGE,"3zsQ1Kl9-2ynF-8LIN-0dku-r61PIn4XyDqG"),sQuery(id+"F18.wireOp",EDGE,"UXQkqX4z-jOis-0Iwp-P2ix-A9E3pHhtgsOQ"),sQuery(id+"F18.wireOp",EDGE,"E115"),sQuery(id+"F18.wireOp",EDGE,"LeDl9sKz-5wQR-wnus-53VY-3W6SMz2K6K2i"),sQuery(id+"F18.wireOp",EDGE,"1wH7Y6pB-1Br9-c6Mt-ri01-EdgmEcDOcEDC")])]});
            var Q1;
            Q1=makeQuery(id+"F19.opExtrude","SWEPT_FACE",FACE,{"disambiguationData":[OSD([sQuery(id+"F18.wireOp",EDGE,"E113.bottom")])]});
            mirror(context, id + "F20", {"operationType" : NewBodyOperationType.ADD, "entities" : qUnion([Q0]), "mirrorPlane" : qUnion([Q1])});
        }
        {
            var Q0;
            Q0=qCreatedBy(makeId("Top.planeOp"),FACE);
            cPlane(context, id + "F21", {"entities" : qUnion([Q0]), "cplaneType" : CPlaneType.OFFSET, "offset" : 153 * mm, "oppositeDirection" : true, "width" : 150 * mm, "height" : 150 * mm});
        }
        {
            var Q0;
            Q0=qCreatedBy(id+"F21.planeOp",FACE);
            var sketch = newSketch(context, id + "F22", { "sketchPlane" : qUnion([Q0])});
            skLineSegment(sketch, "E125.bottom", {"start": v(-72.92, 25.42) * mm, "end": v(73.08, 25.42) * mm});
            skLineSegment(sketch, "E125.top", {"start": v(-72.92, 116.92) * mm, "end": v(73.08, 116.92) * mm});
            skLineSegment(sketch, "E125.left", {"start": v(-72.92, 25.42) * mm, "end": v(-72.92, 116.92) * mm});
            skLineSegment(sketch, "E125.right", {"start": v(73.08, 25.42) * mm, "end": v(73.08, 116.92) * mm});
            skLineSegment(sketch, "E126", {"start": v(-63.92, 25.42) * mm, "end": v(-68.92, 30.42) * mm});
            skLineSegment(sketch, "E127", {"start": v(69.08, 30.42) * mm, "end": v(64.08, 25.42) * mm});
            skLineSegment(sketch, "E128", {"start": v(69.08, 30.42) * mm, "end": v(73.08, 30.42) * mm});
            skLineSegment(sketch, "E129", {"start": v(-68.92, 30.42) * mm, "end": v(-72.92, 30.42) * mm});
            skLineSegment(sketch, "E130", {"start": v(39.08, 25.42) * mm, "end": v(34.08, 30.42) * mm});
            skLineSegment(sketch, "E131", {"start": v(34.08, 30.42) * mm, "end": v(-33.92, 30.42) * mm});
            skLineSegment(sketch, "E132", {"start": v(-33.92, 30.42) * mm, "end": v(-38.92, 25.42) * mm});
            skLineSegment(sketch, "E133", {"start": v(-62.92, 25.42) * mm, "end": v(-62.92, 31.42) * mm, "construction": true});
            skCircle(sketch, "E134", {"center": v(-62.92, 31.42) * mm, "radius": 1.6 * mm});
            skLineSegment(sketch, "E135", {"start": v(63.08, 25.42) * mm, "end": v(63.08, 31.42) * mm, "construction": true});
            skCircle(sketch, "E136", {"center": v(63.08, 31.42) * mm, "radius": 1.6 * mm});
            skSolve(sketch);
        }
        {
            var Q0;
            {var subQ1=sQuery(id+"F22.wireOp",EDGE,"E125.top");Q0=makeQuery(id+"F22.imprint","IMPRINT",FACE,{"disambiguationData":[TD([[makeQuery(id+"F22.imprint","IMPRINT",EDGE,{"derivedFrom":subQ1}),-1.0]])]});}
            extrude(context, id + "F23", {"entities" : qUnion([Q0]), "depth" : 3 * mm});
        }
        {
            var Q0;
            Q0=makeQuery(id+"F23.opExtrude","SWEPT_BODY",BODY,{"disambiguationData":[OSD([sQuery(id+"F22.wireOp",EDGE,"E125.bottom"),sQuery(id+"F22.wireOp",EDGE,"E125.top"),sQuery(id+"F22.wireOp",EDGE,"E125.left"),sQuery(id+"F22.wireOp",EDGE,"E125.right"),sQuery(id+"F22.wireOp",EDGE,"E126"),sQuery(id+"F22.wireOp",EDGE,"dnEH7a7q-0e2G-ZF1u-gQp3-ZGx2YlrUhsfq"),sQuery(id+"F22.wireOp",EDGE,"EYcrjZ5U-B8Tu-Hvld-BROV-cSRqyUUC4nfP"),sQuery(id+"F22.wireOp",EDGE,"lcQWckg9-mZXk-lsL4-PW7S-RH1iYC4EfrxX"),sQuery(id+"F22.wireOp",EDGE,"m4YSihPu-nfU7-MdAm-Gg2Q-VAeN7eaJ9XWN"),sQuery(id+"F22.wireOp",EDGE,"E127")])]});
            var Q1;
            Q1=makeQuery(id+"F23.opExtrude","SWEPT_FACE",FACE,{"disambiguationData":[OSD([sQuery(id+"F22.wireOp",EDGE,"E125.top")])]});
            mirror(context, id + "F24", {"operationType" : NewBodyOperationType.ADD, "entities" : qUnion([Q0]), "mirrorPlane" : qUnion([Q1])});
        }
        {
            var Q0;
            Q0=qCreatedBy(makeId("Front.planeOp"),FACE);
            cPlane(context, id + "F25", {"entities" : qUnion([Q0]), "cplaneType" : CPlaneType.OFFSET, "offset" : 376 * mm, "oppositeDirection" : true, "width" : 150 * mm, "height" : 150 * mm});
        }
        {
            var Q0;
            Q0=qCreatedBy(id+"F25.planeOp",FACE);
            var sketch = newSketch(context, id + "F26", { "sketchPlane" : qUnion([Q0])});
            skLineSegment(sketch, "E137.bottom", {"start": v(-68, 122.5) * mm, "end": v(78, 122.5) * mm});
            skLineSegment(sketch, "E137.top", {"start": v(-68, 9.5) * mm, "end": v(78, 9.5) * mm});
            skLineSegment(sketch, "E137.left", {"start": v(-68, 122.5) * mm, "end": v(-68, 9.5) * mm});
            skLineSegment(sketch, "E137.right", {"start": v(78, 122.5) * mm, "end": v(78, 9.5) * mm});
            skLineSegment(sketch, "E138", {"start": v(-68, 113.5) * mm, "end": v(-64, 113.5) * mm});
            skLineSegment(sketch, "E139", {"start": v(-64, 113.5) * mm, "end": v(-59, 118.5) * mm});
            skLineSegment(sketch, "E140", {"start": v(68, 122.5) * mm, "end": v(68, 112.5) * mm, "construction": true});
            skCircle(sketch, "E141", {"center": v(68, 112.5) * mm, "radius": 1.6 * mm});
            skLineSegment(sketch, "E142", {"start": v(-58, 122.5) * mm, "end": v(-58, 112.5) * mm, "construction": true});
            skCircle(sketch, "E143", {"center": v(-58, 112.5) * mm, "radius": 1.6 * mm});
            skLineSegment(sketch, "E144", {"start": v(78, 113.5) * mm, "end": v(74, 113.5) * mm});
            skLineSegment(sketch, "E145", {"start": v(74, 113.5) * mm, "end": v(69, 118.5) * mm});
            skLineSegment(sketch, "E146", {"start": v(69, 118.5) * mm, "end": v(-59, 118.5) * mm});
            skSolve(sketch);
        }
        {
            var Q0;
            {var subQ1=sQuery(id+"F26.wireOp",EDGE,"E137.top");Q0=makeQuery(id+"F26.imprint","IMPRINT",FACE,{"disambiguationData":[TD([[makeQuery(id+"F26.imprint","IMPRINT",EDGE,{"derivedFrom":subQ1}),1.0]])]});}
            extrude(context, id + "F27", {"entities" : qUnion([Q0]), "depth" : 3 * mm});
        }
        {
            var Q0;
            Q0=makeQuery(id+"F27.opExtrude","SWEPT_BODY",BODY,{"disambiguationData":[OSD([sQuery(id+"F26.wireOp",EDGE,"E137.bottom"),sQuery(id+"F26.wireOp",EDGE,"E137.top"),sQuery(id+"F26.wireOp",EDGE,"E137.left"),sQuery(id+"F26.wireOp",EDGE,"E137.right"),sQuery(id+"F26.wireOp",EDGE,"E138"),sQuery(id+"F26.wireOp",EDGE,"E139"),sQuery(id+"F26.wireOp",EDGE,"ccf2e9e3-9b64-4f2a-9f18-310bc790516a"),sQuery(id+"F26.wireOp",EDGE,"c5f426b9-73f2-4868-9408-4cfd947a191f"),sQuery(id+"F26.wireOp",EDGE,"cd8d91dd-9a42-4ae4-8430-5a7eccad3886"),sQuery(id+"F26.wireOp",EDGE,"f1dcae7c-8bd8-43e5-b7b1-ff3532f110ef")])]});
            var Q1;
            Q1=makeQuery(id+"F27.opExtrude","SWEPT_FACE",FACE,{"disambiguationData":[OSD([sQuery(id+"F26.wireOp",EDGE,"E137.top")])]});
            mirror(context, id + "F28", {"operationType" : NewBodyOperationType.ADD, "entities" : qUnion([Q0]), "mirrorPlane" : qUnion([Q1])});
        }
        {
            var Q0;
            {var subQ0=makeQuery(id+"F27.opExtrude","CAP_FACE",FACE,{"disambiguationData":[OSD([sQuery(id+"F26.wireOp",EDGE,"E137.bottom"),sQuery(id+"F26.wireOp",EDGE,"E137.top"),sQuery(id+"F26.wireOp",EDGE,"E137.left"),sQuery(id+"F26.wireOp",EDGE,"E137.right"),sQuery(id+"F26.wireOp",EDGE,"E138"),sQuery(id+"F26.wireOp",EDGE,"E139"),sQuery(id+"F26.wireOp",EDGE,"ccf2e9e3-9b64-4f2a-9f18-310bc790516a"),sQuery(id+"F26.wireOp",EDGE,"c5f426b9-73f2-4868-9408-4cfd947a191f"),sQuery(id+"F26.wireOp",EDGE,"cd8d91dd-9a42-4ae4-8430-5a7eccad3886"),sQuery(id+"F26.wireOp",EDGE,"f1dcae7c-8bd8-43e5-b7b1-ff3532f110ef")])],"isStart":true});Q0=makeQuery(id+"F28.boolean.opBoolean","MERGE",FACE,{"derivedFrom":[subQ0,makeQuery(id+"F28.opPattern","COPY",FACE,{"derivedFrom":subQ0,"instanceName":"1"})]});}
            var sketch = newSketch(context, id + "F29", { "sketchPlane" : qUnion([Q0])});
            skLineSegment(sketch, "E147", {"start": v(-67, 105.5) * mm, "end": v(-67, -64.5) * mm, "construction": true});
            skLineSegment(sketch, "E148", {"start": v(-67, -64.5) * mm, "end": v(-78, -64.5) * mm, "construction": true});
            skLineSegment(sketch, "E149", {"start": v(-67, -63.2) * mm, "end": v(-58.9, -63.2) * mm, "construction": true});
            skLineSegment(sketch, "E150.bottom", {"start": v(-58.9, -71.15) * mm, "end": v(37.5, -71.15) * mm});
            skLineSegment(sketch, "E150.top", {"start": v(-58.9, -55.25) * mm, "end": v(37.5, -55.25) * mm});
            skLineSegment(sketch, "E150.left", {"start": v(-58.9, -71.15) * mm, "end": v(-58.9, -55.25) * mm});
            skLineSegment(sketch, "E150.right", {"start": v(37.5, -71.15) * mm, "end": v(37.5, -55.25) * mm});
            skLineSegment(sketch, "E151.bottom", {"start": v(-58.9, -75.55) * mm, "end": v(37.5, -75.55) * mm});
            skLineSegment(sketch, "E151.top", {"start": v(-58.9, -91.45) * mm, "end": v(37.5, -91.45) * mm});
            skLineSegment(sketch, "E151.left", {"start": v(-58.9, -75.55) * mm, "end": v(-58.9, -91.45) * mm});
            skLineSegment(sketch, "E151.right", {"start": v(37.5, -75.55) * mm, "end": v(37.5, -91.45) * mm});
            skLineSegment(sketch, "E152", {"start": v(37.5, -75.55) * mm, "end": v(37.5, -71.15) * mm, "construction": true});
            skLineSegment(sketch, "E153.bottom", {"start": v(-24.6, 108.1) * mm, "end": v(-69.3, 108.1) * mm});
            skLineSegment(sketch, "E154", {"start": v(-69.3, 108.1) * mm, "end": v(-69.3, -50.9) * mm});
            skLineSegment(sketch, "E155", {"start": v(-69.3, -50.9) * mm, "end": v(-24.6, -50.9) * mm});
            skLineSegment(sketch, "E156", {"start": v(-24.6, -50.9) * mm, "end": v(-24.6, 108.1) * mm});
            skArc(sketch, "E157", {"start": v(-68.55, 108.1) * mm, "mid": v(-69.83, 108.63) * mm, "end": v(-69.3, 107.35) * mm});
            skArc(sketch, "E158", {"start": v(-24.6, 107.35) * mm, "mid": v(-24.07, 108.63) * mm, "end": v(-25.35, 108.1) * mm});
            skArc(sketch, "E159", {"start": v(-69.3, -50.15) * mm, "mid": v(-69.83, -51.43) * mm, "end": v(-68.55, -50.9) * mm});
            skLineSegment(sketch, "E160", {"start": v(42.5, -50.75) * mm, "end": v(42.5, -90.75) * mm});
            skLineSegment(sketch, "E161", {"start": v(37.5, -55.25) * mm, "end": v(42.5, -55.25) * mm, "construction": true});
            skLineSegment(sketch, "E162", {"start": v(42.5, -90.75) * mm, "end": v(60.5, -90.75) * mm});
            skLineSegment(sketch, "E163", {"start": v(-69, -99.5) * mm, "end": v(-78, -99.5) * mm, "construction": true});
            skLineSegment(sketch, "E164", {"start": v(60.5, -50.75) * mm, "end": v(60.5, -90.75) * mm});
            skLineSegment(sketch, "E165", {"start": v(42.5, -50.75) * mm, "end": v(48.5, -50.75) * mm});
            skLineSegment(sketch, "E166", {"start": v(48.5, -50.75) * mm, "end": v(51.5, -47.75) * mm});
            skLineSegment(sketch, "E167", {"start": v(51.5, -47.75) * mm, "end": v(60.5, -47.75) * mm});
            skLineSegment(sketch, "E168", {"start": v(60.5, -47.75) * mm, "end": v(60.5, -50.75) * mm});
            skLineSegment(sketch, "E169", {"start": v(50.5, -47.75) * mm, "end": v(50.5, -42.75) * mm, "construction": true});
            skLineSegment(sketch, "E170", {"start": v(51.5, -90.75) * mm, "end": v(51.5, -95.75) * mm, "construction": true});
            skLineSegment(sketch, "E171", {"start": v(48.5, -50.75) * mm, "end": v(60.5, -50.75) * mm, "construction": true});
            skLineSegment(sketch, "E172", {"start": v(50.5, -42.75) * mm, "end": v(52.5, -42.75) * mm, "construction": true});
            skArc(sketch, "E173.0.startCap", {"start": v(50.5, -44.35) * mm, "mid": v(48.9, -42.75) * mm, "end": v(50.5, -41.15) * mm});
            skArc(sketch, "E173.0.endCap", {"start": v(52.5, -41.15) * mm, "mid": v(54.1, -42.75) * mm, "end": v(52.5, -44.35) * mm});
            skLineSegment(sketch, "E173.0.left", {"start": v(50.5, -41.15) * mm, "end": v(52.5, -41.15) * mm});
            skLineSegment(sketch, "E173.0.right", {"start": v(50.5, -44.35) * mm, "end": v(52.5, -44.35) * mm});
            skLineSegment(sketch, "E174", {"start": v(51.5, -95.75) * mm, "end": v(53.5, -95.75) * mm, "construction": true});
            skArc(sketch, "E175.0.startCap", {"start": v(51.5, -97.35) * mm, "mid": v(49.9, -95.75) * mm, "end": v(51.5, -94.15) * mm});
            skArc(sketch, "E175.0.endCap", {"start": v(53.5, -94.15) * mm, "mid": v(55.1, -95.75) * mm, "end": v(53.5, -97.35) * mm});
            skLineSegment(sketch, "E175.0.left", {"start": v(51.5, -94.15) * mm, "end": v(53.5, -94.15) * mm});
            skLineSegment(sketch, "E175.0.right", {"start": v(51.5, -97.35) * mm, "end": v(53.5, -97.35) * mm});
            skArc(sketch, "E176", {"start": v(-25.35, -50.9) * mm, "mid": v(-24.07, -51.43) * mm, "end": v(-24.6, -50.15) * mm});
            skSolve(sketch);
        }
        {
            var Q0;
            {var subQ0=makeQuery(id+"F27.opExtrude","CAP_FACE",FACE,{"disambiguationData":[OSD([sQuery(id+"F26.wireOp",EDGE,"E137.bottom"),sQuery(id+"F26.wireOp",EDGE,"E137.top"),sQuery(id+"F26.wireOp",EDGE,"E137.left"),sQuery(id+"F26.wireOp",EDGE,"E137.right"),sQuery(id+"F26.wireOp",EDGE,"E138"),sQuery(id+"F26.wireOp",EDGE,"E139"),sQuery(id+"F26.wireOp",EDGE,"ccf2e9e3-9b64-4f2a-9f18-310bc790516a"),sQuery(id+"F26.wireOp",EDGE,"c5f426b9-73f2-4868-9408-4cfd947a191f"),sQuery(id+"F26.wireOp",EDGE,"cd8d91dd-9a42-4ae4-8430-5a7eccad3886"),sQuery(id+"F26.wireOp",EDGE,"f1dcae7c-8bd8-43e5-b7b1-ff3532f110ef")])],"isStart":true});Q0=makeQuery(id+"F28.boolean.opBoolean","MERGE",FACE,{"derivedFrom":[subQ0,makeQuery(id+"F28.opPattern","COPY",FACE,{"derivedFrom":subQ0,"instanceName":"1"})]});}
            var sketch = newSketch(context, id + "F30", { "sketchPlane" : qUnion([Q0])});
            skLineSegment(sketch, "E177", {"start": v(-7.75, 66.5) * mm, "end": v(-7.75, 42.5) * mm, "construction": true});
            skLineSegment(sketch, "E178", {"start": v(-7.75, 42.5) * mm, "end": v(-7.75, 27.5) * mm, "construction": true});
            skLineSegment(sketch, "E179", {"start": v(-7.75, 27.5) * mm, "end": v(-7.75, 3.5) * mm, "construction": true});
            skLineSegment(sketch, "E180", {"start": v(-7.75, 3.5) * mm, "end": v(-7.75, -11.5) * mm, "construction": true});
            skLineSegment(sketch, "E181", {"start": v(-7.75, -11.5) * mm, "end": v(-7.75, -35.5) * mm, "construction": true});
            skArc(sketch, "E182.0.startCap", {"start": v(-11.75, 66.5) * mm, "mid": v(-7.75, 70.5) * mm, "end": v(-3.75, 66.5) * mm});
            skArc(sketch, "E182.0.endCap", {"start": v(-3.75, 42.5) * mm, "mid": v(-7.75, 38.5) * mm, "end": v(-11.75, 42.5) * mm});
            skLineSegment(sketch, "E182.0.left", {"start": v(-3.75, 66.5) * mm, "end": v(-3.75, 42.5) * mm});
            skLineSegment(sketch, "E182.0.right", {"start": v(-11.75, 66.5) * mm, "end": v(-11.75, 42.5) * mm});
            skArc(sketch, "E182.1.startCap", {"start": v(-11.75, 27.5) * mm, "mid": v(-7.75, 31.5) * mm, "end": v(-3.75, 27.5) * mm});
            skArc(sketch, "E182.1.endCap", {"start": v(-3.75, 3.5) * mm, "mid": v(-7.75, -0.5) * mm, "end": v(-11.75, 3.5) * mm});
            skLineSegment(sketch, "E182.1.left", {"start": v(-3.75, 27.5) * mm, "end": v(-3.75, 3.5) * mm});
            skLineSegment(sketch, "E182.1.right", {"start": v(-11.75, 27.5) * mm, "end": v(-11.75, 3.5) * mm});
            skArc(sketch, "E182.2.startCap", {"start": v(-11.75, -11.5) * mm, "mid": v(-7.75, -7.5) * mm, "end": v(-3.75, -11.5) * mm});
            skArc(sketch, "E182.2.endCap", {"start": v(-3.75, -35.5) * mm, "mid": v(-7.75, -39.5) * mm, "end": v(-11.75, -35.5) * mm});
            skLineSegment(sketch, "E182.2.left", {"start": v(-3.75, -11.5) * mm, "end": v(-3.75, -35.5) * mm});
            skLineSegment(sketch, "E182.2.right", {"start": v(-11.75, -11.5) * mm, "end": v(-11.75, -35.5) * mm});
            skLineSegment(sketch, "E183.1.0.0", {"start": v(4.25, 27.5) * mm, "end": v(4.25, 3.5) * mm});
            skArc(sketch, "E183.1.0.1", {"start": v(4.25, -11.5) * mm, "mid": v(8.25, -7.5) * mm, "end": v(12.25, -11.5) * mm});
            skArc(sketch, "E183.1.0.3", {"start": v(4.25, 66.5) * mm, "mid": v(8.25, 70.5) * mm, "end": v(12.25, 66.5) * mm});
            skLineSegment(sketch, "E183.1.0.4", {"start": v(4.25, -11.5) * mm, "end": v(4.25, -35.5) * mm});
            skArc(sketch, "E183.1.0.5", {"start": v(4.25, 27.5) * mm, "mid": v(8.25, 31.5) * mm, "end": v(12.25, 27.5) * mm});
            skArc(sketch, "E183.1.0.6", {"start": v(12.25, -35.5) * mm, "mid": v(8.25, -39.5) * mm, "end": v(4.25, -35.5) * mm});
            skArc(sketch, "E183.1.0.7", {"start": v(12.25, 3.5) * mm, "mid": v(8.25, -0.5) * mm, "end": v(4.25, 3.5) * mm});
            skLineSegment(sketch, "E183.1.0.11", {"start": v(8.25, -11.5) * mm, "end": v(8.25, -35.5) * mm, "construction": true});
            skLineSegment(sketch, "E183.1.0.12", {"start": v(8.25, 3.5) * mm, "end": v(8.25, -11.5) * mm, "construction": true});
            skLineSegment(sketch, "E183.1.0.13", {"start": v(8.25, 27.5) * mm, "end": v(8.25, 3.5) * mm, "construction": true});
            skLineSegment(sketch, "E183.1.0.14", {"start": v(8.25, 42.5) * mm, "end": v(8.25, 27.5) * mm, "construction": true});
            skLineSegment(sketch, "E183.1.0.15", {"start": v(8.25, 66.5) * mm, "end": v(8.25, 42.5) * mm, "construction": true});
            skLineSegment(sketch, "E183.1.0.16", {"start": v(12.25, 27.5) * mm, "end": v(12.25, 3.5) * mm});
            skLineSegment(sketch, "E183.1.0.20", {"start": v(4.25, 66.5) * mm, "end": v(4.25, 42.5) * mm});
            skLineSegment(sketch, "E183.1.0.21", {"start": v(12.25, 66.5) * mm, "end": v(12.25, 42.5) * mm});
            skArc(sketch, "E183.1.0.22", {"start": v(12.25, 42.5) * mm, "mid": v(8.25, 38.5) * mm, "end": v(4.25, 42.5) * mm});
            skLineSegment(sketch, "E183.1.0.23", {"start": v(12.25, -11.5) * mm, "end": v(12.25, -35.5) * mm});
            skLineSegment(sketch, "E183.2.0.0", {"start": v(20.25, 27.5) * mm, "end": v(20.25, 3.5) * mm});
            skArc(sketch, "E183.2.0.1", {"start": v(20.25, -11.5) * mm, "mid": v(24.25, -7.5) * mm, "end": v(28.25, -11.5) * mm});
            skArc(sketch, "E183.2.0.3", {"start": v(20.25, 66.5) * mm, "mid": v(24.25, 70.5) * mm, "end": v(28.25, 66.5) * mm});
            skLineSegment(sketch, "E183.2.0.4", {"start": v(20.25, -11.5) * mm, "end": v(20.25, -35.5) * mm});
            skArc(sketch, "E183.2.0.5", {"start": v(20.25, 27.5) * mm, "mid": v(24.25, 31.5) * mm, "end": v(28.25, 27.5) * mm});
            skArc(sketch, "E183.2.0.6", {"start": v(28.25, -35.5) * mm, "mid": v(24.25, -39.5) * mm, "end": v(20.25, -35.5) * mm});
            skArc(sketch, "E183.2.0.7", {"start": v(28.25, 3.5) * mm, "mid": v(24.25, -0.5) * mm, "end": v(20.25, 3.5) * mm});
            skLineSegment(sketch, "E183.2.0.11", {"start": v(24.25, -11.5) * mm, "end": v(24.25, -35.5) * mm, "construction": true});
            skLineSegment(sketch, "E183.2.0.12", {"start": v(24.25, 3.5) * mm, "end": v(24.25, -11.5) * mm, "construction": true});
            skLineSegment(sketch, "E183.2.0.13", {"start": v(24.25, 27.5) * mm, "end": v(24.25, 3.5) * mm, "construction": true});
            skLineSegment(sketch, "E183.2.0.14", {"start": v(24.25, 42.5) * mm, "end": v(24.25, 27.5) * mm, "construction": true});
            skLineSegment(sketch, "E183.2.0.15", {"start": v(24.25, 66.5) * mm, "end": v(24.25, 42.5) * mm, "construction": true});
            skLineSegment(sketch, "E183.2.0.16", {"start": v(28.25, 27.5) * mm, "end": v(28.25, 3.5) * mm});
            skLineSegment(sketch, "E183.2.0.20", {"start": v(20.25, 66.5) * mm, "end": v(20.25, 42.5) * mm});
            skLineSegment(sketch, "E183.2.0.21", {"start": v(28.25, 66.5) * mm, "end": v(28.25, 42.5) * mm});
            skArc(sketch, "E183.2.0.22", {"start": v(28.25, 42.5) * mm, "mid": v(24.25, 38.5) * mm, "end": v(20.25, 42.5) * mm});
            skLineSegment(sketch, "E183.2.0.23", {"start": v(28.25, -11.5) * mm, "end": v(28.25, -35.5) * mm});
            skLineSegment(sketch, "E183.direction1", {"start": v(-11.75, -35.5) * mm, "end": v(4.25, -35.5) * mm, "construction": true});
            skLineSegment(sketch, "E184", {"start": v(48, 96.85) * mm, "end": v(68, 96.85) * mm, "construction": true});
            skCircle(sketch, "E185", {"center": v(48, 96.85) * mm, "radius": 6 * mm});
            skLineSegment(sketch, "E186.bottom", {"start": v(-5.75, 108.1) * mm, "end": v(21.75, 108.1) * mm});
            skLineSegment(sketch, "E186.top", {"start": v(-5.75, 85.6) * mm, "end": v(21.75, 85.6) * mm});
            skLineSegment(sketch, "E186.left", {"start": v(-7.75, 106.1) * mm, "end": v(-7.75, 87.6) * mm});
            skLineSegment(sketch, "E186.right", {"start": v(23.75, 106.1) * mm, "end": v(23.75, 87.6) * mm});
            skLineSegment(sketch, "E187", {"start": v(8, 108.1) * mm, "end": v(8, 118.5) * mm, "construction": true});
            skLineSegment(sketch, "E188", {"start": v(-7.75, 96.85) * mm, "end": v(-12, 96.85) * mm, "construction": true});
            skLineSegment(sketch, "E189", {"start": v(23.75, 96.85) * mm, "end": v(28, 96.85) * mm, "construction": true});
            skCircle(sketch, "E190", {"center": v(-12, 96.85) * mm, "radius": 1.6 * mm});
            skCircle(sketch, "E191", {"center": v(28, 96.85) * mm, "radius": 1.6 * mm});
            skPoint(sketch, "E192.visualSharp", {"position": v(-7.75, 108.1) * mm});
            skArc(sketch, "E192.filletArc", {"start": v(-5.75, 108.1) * mm, "mid": v(-7.16, 107.51) * mm, "end": v(-7.75, 106.1) * mm});
            skPoint(sketch, "E193.visualSharp", {"position": v(23.75, 108.1) * mm});
            skArc(sketch, "E193.filletArc", {"start": v(23.75, 106.1) * mm, "mid": v(23.16, 107.51) * mm, "end": v(21.75, 108.1) * mm});
            skPoint(sketch, "E194.visualSharp", {"position": v(-7.75, 85.6) * mm});
            skArc(sketch, "E194.filletArc", {"start": v(-7.75, 87.6) * mm, "mid": v(-7.16, 86.18) * mm, "end": v(-5.75, 85.6) * mm});
            skPoint(sketch, "E195.visualSharp", {"position": v(23.75, 85.6) * mm});
            skArc(sketch, "E195.filletArc", {"start": v(21.75, 85.6) * mm, "mid": v(23.16, 86.18) * mm, "end": v(23.75, 87.6) * mm});
            skLineSegment(sketch, "E196", {"start": v(28, 96.85) * mm, "end": v(48, 96.85) * mm, "construction": true});
            skLineSegment(sketch, "E197", {"start": v(-7.75, -35.5) * mm, "end": v(-78, -35.5) * mm, "construction": true});
            skSolve(sketch);
        }
        {
            var Q0;
            Q0=qSketchRegion(id+"F29",true);
            var Q1;
            Q1=qSketchRegion(id+"F30",true);
            extrude(context, id + "F31", {"entities" : qUnion([Q0, Q1]), "operationType" : NewBodyOperationType.REMOVE, "oppositeDirection" : true, "depth" : 25 * mm});
        }
        {
            var Q0;
            Q0=makeQuery(id+"F31.boolean.opBoolean","COPY",EDGE,{"derivedFrom":makeQuery(id+"F31.opExtrude","SWEPT_EDGE",EDGE,{"disambiguationData":[OSD([sQuery(id+"F29.wireOp",EDGE,"E150.top"),sQuery(id+"F29.wireOp",EDGE,"E150.left")])]})});
            var Q1;
            Q1=makeQuery(id+"F31.boolean.opBoolean","COPY",EDGE,{"derivedFrom":makeQuery(id+"F31.opExtrude","SWEPT_EDGE",EDGE,{"disambiguationData":[OSD([sQuery(id+"F29.wireOp",EDGE,"E150.bottom"),sQuery(id+"F29.wireOp",EDGE,"E150.left")])]})});
            var Q2;
            Q2=makeQuery(id+"F31.boolean.opBoolean","COPY",EDGE,{"derivedFrom":makeQuery(id+"F31.opExtrude","SWEPT_EDGE",EDGE,{"disambiguationData":[OSD([sQuery(id+"F29.wireOp",EDGE,"E151.bottom"),sQuery(id+"F29.wireOp",EDGE,"E151.left")])]})});
            var Q3;
            Q3=makeQuery(id+"F31.boolean.opBoolean","COPY",EDGE,{"derivedFrom":makeQuery(id+"F31.opExtrude","SWEPT_EDGE",EDGE,{"disambiguationData":[OSD([sQuery(id+"F29.wireOp",EDGE,"E151.top"),sQuery(id+"F29.wireOp",EDGE,"E151.left")])]})});
            var Q4;
            Q4=makeQuery(id+"F31.boolean.opBoolean","COPY",EDGE,{"derivedFrom":makeQuery(id+"F31.opExtrude","SWEPT_EDGE",EDGE,{"disambiguationData":[OSD([sQuery(id+"F29.wireOp",EDGE,"E151.top"),sQuery(id+"F29.wireOp",EDGE,"E151.right")])]})});
            var Q5;
            Q5=makeQuery(id+"F31.boolean.opBoolean","COPY",EDGE,{"derivedFrom":makeQuery(id+"F31.opExtrude","SWEPT_EDGE",EDGE,{"disambiguationData":[OSD([sQuery(id+"F29.wireOp",EDGE,"E151.bottom"),sQuery(id+"F29.wireOp",EDGE,"E151.right")])]})});
            var Q6;
            Q6=makeQuery(id+"F31.boolean.opBoolean","COPY",EDGE,{"derivedFrom":makeQuery(id+"F31.opExtrude","SWEPT_EDGE",EDGE,{"disambiguationData":[OSD([sQuery(id+"F29.wireOp",EDGE,"E150.bottom"),sQuery(id+"F29.wireOp",EDGE,"E150.right")])]})});
            var Q7;
            Q7=makeQuery(id+"F31.boolean.opBoolean","COPY",EDGE,{"derivedFrom":makeQuery(id+"F31.opExtrude","SWEPT_EDGE",EDGE,{"disambiguationData":[OSD([sQuery(id+"F29.wireOp",EDGE,"E150.top"),sQuery(id+"F29.wireOp",EDGE,"E150.right")])]})});
            chamfer(context, id + "F32", {"entities" : qUnion([Q0, Q1, Q2, Q3, Q4, Q5, Q6, Q7]), "width" : 2 * mm, "tangentPropagation" : true});
        }
        {
            var Q0;
            {var subQ0=makeQuery(id+"F19.opExtrude","CAP_FACE",FACE,{"disambiguationData":[OSD([sQuery(id+"F18.wireOp",EDGE,"E113.bottom"),sQuery(id+"F18.wireOp",EDGE,"E113.top"),sQuery(id+"F18.wireOp",EDGE,"E113.left"),sQuery(id+"F18.wireOp",EDGE,"E113.right"),sQuery(id+"F18.wireOp",EDGE,"E114"),sQuery(id+"F18.wireOp",EDGE,"E115"),sQuery(id+"F18.wireOp",EDGE,"E116"),sQuery(id+"F18.wireOp",EDGE,"E117")])],"isStart":false});Q0=makeQuery(id+"F20.boolean.opBoolean","MERGE",FACE,{"derivedFrom":[subQ0,makeQuery(id+"F20.opPattern","COPY",FACE,{"derivedFrom":subQ0,"instanceName":"1"})]});}
            var sketch = newSketch(context, id + "F33", { "sketchPlane" : qUnion([Q0])});
            skLineSegment(sketch, "E198", {"start": v(29.98, 246.87) * mm, "end": v(29.98, 223.62) * mm, "construction": true});
            skLineSegment(sketch, "E199", {"start": v(29.98, 223.62) * mm, "end": v(44.98, 223.62) * mm, "construction": true});
            skArc(sketch, "E200.0.startCap", {"start": v(29.98, 221.12) * mm, "mid": v(27.48, 223.62) * mm, "end": v(29.98, 226.12) * mm});
            skArc(sketch, "E200.0.endCap", {"start": v(44.98, 226.12) * mm, "mid": v(47.48, 223.62) * mm, "end": v(44.98, 221.12) * mm});
            skLineSegment(sketch, "E200.0.left", {"start": v(29.98, 226.12) * mm, "end": v(44.98, 226.12) * mm});
            skLineSegment(sketch, "E200.0.right", {"start": v(29.98, 221.12) * mm, "end": v(44.98, 221.12) * mm});
            skLineSegment(sketch, "E201.0.1.0", {"start": v(29.98, 211.12) * mm, "end": v(44.98, 211.12) * mm});
            skLineSegment(sketch, "E201.0.1.1", {"start": v(29.98, 216.12) * mm, "end": v(44.98, 216.12) * mm});
            skArc(sketch, "E201.0.1.2", {"start": v(29.98, 211.12) * mm, "mid": v(27.48, 213.62) * mm, "end": v(29.98, 216.12) * mm});
            skLineSegment(sketch, "E201.0.1.3", {"start": v(29.98, 213.62) * mm, "end": v(44.98, 213.62) * mm, "construction": true});
            skArc(sketch, "E201.0.1.4", {"start": v(44.98, 216.12) * mm, "mid": v(47.48, 213.62) * mm, "end": v(44.98, 211.12) * mm});
            skLineSegment(sketch, "E201.0.2.0", {"start": v(29.98, 201.12) * mm, "end": v(44.98, 201.12) * mm});
            skLineSegment(sketch, "E201.0.2.1", {"start": v(29.98, 206.12) * mm, "end": v(44.98, 206.12) * mm});
            skArc(sketch, "E201.0.2.2", {"start": v(29.98, 201.12) * mm, "mid": v(27.48, 203.62) * mm, "end": v(29.98, 206.12) * mm});
            skLineSegment(sketch, "E201.0.2.3", {"start": v(29.98, 203.62) * mm, "end": v(44.98, 203.62) * mm, "construction": true});
            skArc(sketch, "E201.0.2.4", {"start": v(44.98, 206.12) * mm, "mid": v(47.48, 203.62) * mm, "end": v(44.98, 201.12) * mm});
            skLineSegment(sketch, "E201.0.3.0", {"start": v(29.98, 191.12) * mm, "end": v(44.98, 191.12) * mm});
            skLineSegment(sketch, "E201.0.3.1", {"start": v(29.98, 196.12) * mm, "end": v(44.98, 196.12) * mm});
            skArc(sketch, "E201.0.3.2", {"start": v(29.98, 191.12) * mm, "mid": v(27.48, 193.62) * mm, "end": v(29.98, 196.12) * mm});
            skLineSegment(sketch, "E201.0.3.3", {"start": v(29.98, 193.62) * mm, "end": v(44.98, 193.62) * mm, "construction": true});
            skArc(sketch, "E201.0.3.4", {"start": v(44.98, 196.12) * mm, "mid": v(47.48, 193.62) * mm, "end": v(44.98, 191.12) * mm});
            skLineSegment(sketch, "E201.0.4.0", {"start": v(29.98, 181.12) * mm, "end": v(44.98, 181.12) * mm});
            skLineSegment(sketch, "E201.0.4.1", {"start": v(29.98, 186.12) * mm, "end": v(44.98, 186.12) * mm});
            skArc(sketch, "E201.0.4.2", {"start": v(29.98, 181.12) * mm, "mid": v(27.48, 183.62) * mm, "end": v(29.98, 186.12) * mm});
            skLineSegment(sketch, "E201.0.4.3", {"start": v(29.98, 183.62) * mm, "end": v(44.98, 183.62) * mm, "construction": true});
            skArc(sketch, "E201.0.4.4", {"start": v(44.98, 186.12) * mm, "mid": v(47.48, 183.62) * mm, "end": v(44.98, 181.12) * mm});
            skLineSegment(sketch, "E201.0.5.0", {"start": v(29.98, 171.12) * mm, "end": v(44.98, 171.12) * mm});
            skLineSegment(sketch, "E201.0.5.1", {"start": v(29.98, 176.12) * mm, "end": v(44.98, 176.12) * mm});
            skArc(sketch, "E201.0.5.2", {"start": v(29.98, 171.12) * mm, "mid": v(27.48, 173.62) * mm, "end": v(29.98, 176.12) * mm});
            skLineSegment(sketch, "E201.0.5.3", {"start": v(29.98, 173.62) * mm, "end": v(44.98, 173.62) * mm, "construction": true});
            skArc(sketch, "E201.0.5.4", {"start": v(44.98, 176.12) * mm, "mid": v(47.48, 173.62) * mm, "end": v(44.98, 171.12) * mm});
            skLineSegment(sketch, "E201.0.6.0", {"start": v(29.98, 161.12) * mm, "end": v(44.98, 161.12) * mm});
            skLineSegment(sketch, "E201.0.6.1", {"start": v(29.98, 166.12) * mm, "end": v(44.98, 166.12) * mm});
            skArc(sketch, "E201.0.6.2", {"start": v(29.98, 161.12) * mm, "mid": v(27.48, 163.62) * mm, "end": v(29.98, 166.12) * mm});
            skLineSegment(sketch, "E201.0.6.3", {"start": v(29.98, 163.62) * mm, "end": v(44.98, 163.62) * mm, "construction": true});
            skArc(sketch, "E201.0.6.4", {"start": v(44.98, 166.12) * mm, "mid": v(47.48, 163.62) * mm, "end": v(44.98, 161.12) * mm});
            skLineSegment(sketch, "E201.0.7.0", {"start": v(29.98, 151.12) * mm, "end": v(44.98, 151.12) * mm});
            skLineSegment(sketch, "E201.0.7.1", {"start": v(29.98, 156.12) * mm, "end": v(44.98, 156.12) * mm});
            skArc(sketch, "E201.0.7.2", {"start": v(29.98, 151.12) * mm, "mid": v(27.48, 153.62) * mm, "end": v(29.98, 156.12) * mm});
            skLineSegment(sketch, "E201.0.7.3", {"start": v(29.98, 153.62) * mm, "end": v(44.98, 153.62) * mm, "construction": true});
            skArc(sketch, "E201.0.7.4", {"start": v(44.98, 156.12) * mm, "mid": v(47.48, 153.62) * mm, "end": v(44.98, 151.12) * mm});
            skLineSegment(sketch, "E201.0.8.0", {"start": v(29.98, 141.12) * mm, "end": v(44.98, 141.12) * mm});
            skLineSegment(sketch, "E201.0.8.1", {"start": v(29.98, 146.12) * mm, "end": v(44.98, 146.12) * mm});
            skArc(sketch, "E201.0.8.2", {"start": v(29.98, 141.12) * mm, "mid": v(27.48, 143.62) * mm, "end": v(29.98, 146.12) * mm});
            skLineSegment(sketch, "E201.0.8.3", {"start": v(29.98, 143.62) * mm, "end": v(44.98, 143.62) * mm, "construction": true});
            skArc(sketch, "E201.0.8.4", {"start": v(44.98, 146.12) * mm, "mid": v(47.48, 143.62) * mm, "end": v(44.98, 141.12) * mm});
            skLineSegment(sketch, "E201.0.9.0", {"start": v(29.98, 131.12) * mm, "end": v(44.98, 131.12) * mm});
            skLineSegment(sketch, "E201.0.9.1", {"start": v(29.98, 136.12) * mm, "end": v(44.98, 136.12) * mm});
            skArc(sketch, "E201.0.9.2", {"start": v(29.98, 131.12) * mm, "mid": v(27.48, 133.62) * mm, "end": v(29.98, 136.12) * mm});
            skLineSegment(sketch, "E201.0.9.3", {"start": v(29.98, 133.62) * mm, "end": v(44.98, 133.62) * mm, "construction": true});
            skArc(sketch, "E201.0.9.4", {"start": v(44.98, 136.12) * mm, "mid": v(47.48, 133.62) * mm, "end": v(44.98, 131.12) * mm});
            skLineSegment(sketch, "E201.0.10.0", {"start": v(29.98, 121.12) * mm, "end": v(44.98, 121.12) * mm});
            skLineSegment(sketch, "E201.0.10.1", {"start": v(29.98, 126.12) * mm, "end": v(44.98, 126.12) * mm});
            skArc(sketch, "E201.0.10.2", {"start": v(29.98, 121.12) * mm, "mid": v(27.48, 123.62) * mm, "end": v(29.98, 126.12) * mm});
            skLineSegment(sketch, "E201.0.10.3", {"start": v(29.98, 123.62) * mm, "end": v(44.98, 123.62) * mm, "construction": true});
            skArc(sketch, "E201.0.10.4", {"start": v(44.98, 126.12) * mm, "mid": v(47.48, 123.62) * mm, "end": v(44.98, 121.12) * mm});
            skLineSegment(sketch, "E201.0.11.0", {"start": v(29.98, 111.12) * mm, "end": v(44.98, 111.12) * mm});
            skLineSegment(sketch, "E201.0.11.1", {"start": v(29.98, 116.12) * mm, "end": v(44.98, 116.12) * mm});
            skArc(sketch, "E201.0.11.2", {"start": v(29.98, 111.12) * mm, "mid": v(27.48, 113.62) * mm, "end": v(29.98, 116.12) * mm});
            skLineSegment(sketch, "E201.0.11.3", {"start": v(29.98, 113.62) * mm, "end": v(44.98, 113.62) * mm, "construction": true});
            skArc(sketch, "E201.0.11.4", {"start": v(44.98, 116.12) * mm, "mid": v(47.48, 113.62) * mm, "end": v(44.98, 111.12) * mm});
            skLineSegment(sketch, "E201.0.12.0", {"start": v(29.98, 101.12) * mm, "end": v(44.98, 101.12) * mm});
            skLineSegment(sketch, "E201.0.12.1", {"start": v(29.98, 106.12) * mm, "end": v(44.98, 106.12) * mm});
            skArc(sketch, "E201.0.12.2", {"start": v(29.98, 101.12) * mm, "mid": v(27.48, 103.62) * mm, "end": v(29.98, 106.12) * mm});
            skLineSegment(sketch, "E201.0.12.3", {"start": v(29.98, 103.62) * mm, "end": v(44.98, 103.62) * mm, "construction": true});
            skArc(sketch, "E201.0.12.4", {"start": v(44.98, 106.12) * mm, "mid": v(47.48, 103.62) * mm, "end": v(44.98, 101.12) * mm});
            skLineSegment(sketch, "E201.0.13.0", {"start": v(29.98, 91.12) * mm, "end": v(44.98, 91.12) * mm});
            skLineSegment(sketch, "E201.0.13.1", {"start": v(29.98, 96.12) * mm, "end": v(44.98, 96.12) * mm});
            skArc(sketch, "E201.0.13.2", {"start": v(29.98, 91.12) * mm, "mid": v(27.48, 93.62) * mm, "end": v(29.98, 96.12) * mm});
            skLineSegment(sketch, "E201.0.13.3", {"start": v(29.98, 93.62) * mm, "end": v(44.98, 93.62) * mm, "construction": true});
            skArc(sketch, "E201.0.13.4", {"start": v(44.98, 96.12) * mm, "mid": v(47.48, 93.62) * mm, "end": v(44.98, 91.12) * mm});
            skLineSegment(sketch, "E201.0.14.0", {"start": v(29.98, 81.12) * mm, "end": v(44.98, 81.12) * mm});
            skLineSegment(sketch, "E201.0.14.1", {"start": v(29.98, 86.12) * mm, "end": v(44.98, 86.12) * mm});
            skArc(sketch, "E201.0.14.2", {"start": v(29.98, 81.12) * mm, "mid": v(27.48, 83.62) * mm, "end": v(29.98, 86.12) * mm});
            skLineSegment(sketch, "E201.0.14.3", {"start": v(29.98, 83.62) * mm, "end": v(44.98, 83.62) * mm, "construction": true});
            skArc(sketch, "E201.0.14.4", {"start": v(44.98, 86.12) * mm, "mid": v(47.48, 83.62) * mm, "end": v(44.98, 81.12) * mm});
            skLineSegment(sketch, "E201.direction1", {"start": v(21.97, 221.12) * mm, "end": v(29.98, 221.12) * mm, "construction": true});
            skLineSegment(sketch, "E201.direction2", {"start": v(29.98, 221.12) * mm, "end": v(29.98, 211.12) * mm, "construction": true});
            skLineSegment(sketch, "E202.bottom", {"start": v(-72.02, 83.02) * mm, "end": v(4.58, 83.02) * mm, "construction": true});
            skLineSegment(sketch, "E202.top", {"start": v(-72.02, 144.72) * mm, "end": v(4.58, 144.72) * mm, "construction": true});
            skLineSegment(sketch, "E202.left", {"start": v(-72.02, 83.02) * mm, "end": v(-72.02, 144.72) * mm, "construction": true});
            skLineSegment(sketch, "E202.right", {"start": v(4.58, 83.02) * mm, "end": v(4.58, 144.72) * mm, "construction": true});
            skLineSegment(sketch, "E203", {"start": v(-72.02, 113.87) * mm, "end": v(-87.02, 113.87) * mm, "construction": true});
            skLineSegment(sketch, "E204.bottom", {"start": v(-72.02, 156.02) * mm, "end": v(4.58, 156.02) * mm, "construction": true});
            skLineSegment(sketch, "E204.top", {"start": v(-72.02, 217.72) * mm, "end": v(4.58, 217.72) * mm, "construction": true});
            skLineSegment(sketch, "E204.left", {"start": v(-72.02, 156.02) * mm, "end": v(-72.02, 217.72) * mm, "construction": true});
            skLineSegment(sketch, "E204.right", {"start": v(4.58, 156.02) * mm, "end": v(4.58, 217.72) * mm, "construction": true});
            skLineSegment(sketch, "E205", {"start": v(-72.02, 186.87) * mm, "end": v(-87.02, 186.87) * mm, "construction": true});
            skCircle(sketch, "E206", {"center": v(4.58, 83.02) * mm, "radius": 1.6 * mm});
            skCircle(sketch, "E207", {"center": v(4.58, 144.72) * mm, "radius": 1.6 * mm});
            skCircle(sketch, "E208", {"center": v(-72.02, 144.72) * mm, "radius": 1.6 * mm});
            skCircle(sketch, "E209", {"center": v(-72.02, 83.02) * mm, "radius": 1.6 * mm});
            skCircle(sketch, "E210", {"center": v(-72.02, 156.02) * mm, "radius": 1.6 * mm});
            skCircle(sketch, "E211", {"center": v(-72.02, 217.72) * mm, "radius": 1.6 * mm});
            skCircle(sketch, "E212", {"center": v(4.58, 217.72) * mm, "radius": 1.6 * mm});
            skCircle(sketch, "E213", {"center": v(4.58, 156.02) * mm, "radius": 1.6 * mm});
            skSolve(sketch);
        }
        {
            var Q0;
            Q0=qSketchRegion(id+"F33",true);
            extrude(context, id + "F34", {"entities" : qUnion([Q0]), "operationType" : NewBodyOperationType.REMOVE, "oppositeDirection" : true, "depth" : 25 * mm});
        }
        {
            var Q0;
            {var subQ0=makeQuery(id+"F23.opExtrude","CAP_FACE",FACE,{"disambiguationData":[OSD([sQuery(id+"F22.wireOp",EDGE,"E125.bottom"),sQuery(id+"F22.wireOp",EDGE,"E125.top"),sQuery(id+"F22.wireOp",EDGE,"E125.left"),sQuery(id+"F22.wireOp",EDGE,"E125.right"),sQuery(id+"F22.wireOp",EDGE,"E126"),sQuery(id+"F22.wireOp",EDGE,"E127"),sQuery(id+"F22.wireOp",EDGE,"E128"),sQuery(id+"F22.wireOp",EDGE,"E129")])],"isStart":true});Q0=makeQuery(id+"F24.boolean.opBoolean","MERGE",FACE,{"derivedFrom":[subQ0,makeQuery(id+"F24.opPattern","COPY",FACE,{"derivedFrom":subQ0,"instanceName":"1"})]});}
            var sketch = newSketch(context, id + "F35", { "sketchPlane" : qUnion([Q0])});
            skLineSegment(sketch, "E214", {"start": v(-57.42, -169.42) * mm, "end": v(57.58, -169.42) * mm, "construction": true});
            skLineSegment(sketch, "E215", {"start": v(-52.42, -169.42) * mm, "end": v(-52.42, -154.42) * mm, "construction": true});
            skLineSegment(sketch, "E216", {"start": v(-52.42, -154.42) * mm, "end": v(-52.42, -120.97) * mm, "construction": true});
            skLineSegment(sketch, "E217", {"start": v(52.58, -169.42) * mm, "end": v(52.58, -154.42) * mm, "construction": true});
            skLineSegment(sketch, "E218", {"start": v(52.58, -154.42) * mm, "end": v(52.58, -123.92) * mm, "construction": true});
            skCircle(sketch, "E219", {"center": v(-52.42, -169.42) * mm, "radius": 2.55 * mm});
            skLineSegment(sketch, "E220", {"start": v(-52.42, -74.42) * mm, "end": v(-52.42, -64.42) * mm, "construction": true});
            skPoint(sketch, "E220.endSnap0", {"position": v(-52.42, -69.1) * mm});
            skCircle(sketch, "E221", {"center": v(-52.42, -64.42) * mm, "radius": 2.55 * mm});
            skLineSegment(sketch, "E222", {"start": v(-52.42, -120.97) * mm, "end": v(-52.42, -107.87) * mm, "construction": true});
            skLineSegment(sketch, "E223", {"start": v(-52.42, -107.87) * mm, "end": v(-52.42, -74.42) * mm, "construction": true});
            skArc(sketch, "E224.0.startCap", {"start": v(-47.42, -154.42) * mm, "mid": v(-52.42, -159.42) * mm, "end": v(-57.42, -154.42) * mm});
            skArc(sketch, "E224.0.endCap", {"start": v(-57.42, -120.97) * mm, "mid": v(-52.42, -115.97) * mm, "end": v(-47.42, -120.97) * mm});
            skLineSegment(sketch, "E224.0.left", {"start": v(-57.42, -154.42) * mm, "end": v(-57.42, -120.97) * mm});
            skLineSegment(sketch, "E224.0.right", {"start": v(-47.42, -154.42) * mm, "end": v(-47.42, -120.97) * mm});
            skArc(sketch, "E224.1.startCap", {"start": v(-47.42, -107.87) * mm, "mid": v(-52.42, -112.87) * mm, "end": v(-57.42, -107.87) * mm});
            skArc(sketch, "E224.1.endCap", {"start": v(-57.42, -74.42) * mm, "mid": v(-52.42, -69.42) * mm, "end": v(-47.42, -74.42) * mm});
            skLineSegment(sketch, "E224.1.left", {"start": v(-57.42, -107.87) * mm, "end": v(-57.42, -74.42) * mm});
            skLineSegment(sketch, "E224.1.right", {"start": v(-47.42, -107.87) * mm, "end": v(-47.42, -74.42) * mm});
            skLineSegment(sketch, "E225", {"start": v(52.58, -123.92) * mm, "end": v(52.58, -109.92) * mm, "construction": true});
            skLineSegment(sketch, "E226", {"start": v(52.58, -109.92) * mm, "end": v(52.58, -79.42) * mm, "construction": true});
            skLineSegment(sketch, "E227", {"start": v(52.58, -79.42) * mm, "end": v(52.58, -64.42) * mm, "construction": true});
            skArc(sketch, "E228.5.startCap", {"start": v(57.58, -154.42) * mm, "mid": v(52.58, -159.42) * mm, "end": v(47.58, -154.42) * mm});
            skArc(sketch, "E228.5.endCap", {"start": v(47.58, -123.92) * mm, "mid": v(52.58, -118.92) * mm, "end": v(57.58, -123.92) * mm});
            skLineSegment(sketch, "E228.5.left", {"start": v(47.58, -154.42) * mm, "end": v(47.58, -123.92) * mm});
            skLineSegment(sketch, "E228.5.right", {"start": v(57.58, -154.42) * mm, "end": v(57.58, -123.92) * mm});
            skArc(sketch, "E228.6.startCap", {"start": v(57.58, -109.92) * mm, "mid": v(52.58, -114.92) * mm, "end": v(47.58, -109.92) * mm});
            skArc(sketch, "E228.6.endCap", {"start": v(47.58, -79.42) * mm, "mid": v(52.58, -74.42) * mm, "end": v(57.58, -79.42) * mm});
            skLineSegment(sketch, "E228.6.left", {"start": v(47.58, -109.92) * mm, "end": v(47.58, -79.42) * mm});
            skLineSegment(sketch, "E228.6.right", {"start": v(57.58, -109.92) * mm, "end": v(57.58, -79.42) * mm});
            skCircle(sketch, "E229", {"center": v(52.58, -169.42) * mm, "radius": 2.55 * mm});
            skCircle(sketch, "E230", {"center": v(52.58, -64.42) * mm, "radius": 2.55 * mm});
            skLineSegment(sketch, "E231", {"start": v(-57.42, -169.42) * mm, "end": v(-57.42, -208.42) * mm, "construction": true});
            skLineSegment(sketch, "E232", {"start": v(-52.42, -64.42) * mm, "end": v(-52.42, -25.42) * mm, "construction": true});
            skLineSegment(sketch, "E233", {"start": v(-39.3, -169.42) * mm, "end": v(-39.3, -143.16) * mm, "construction": true});
            skLineSegment(sketch, "E234", {"start": v(-39.3, -143.16) * mm, "end": v(-39.3, -130.06) * mm, "construction": true});
            skLineSegment(sketch, "E235", {"start": v(-39.3, -130.06) * mm, "end": v(-39.3, -103.8) * mm, "construction": true});
            skLineSegment(sketch, "E236", {"start": v(-39.3, -103.8) * mm, "end": v(-39.3, -90.7) * mm, "construction": true});
            skLineSegment(sketch, "E237", {"start": v(-39.3, -64.42) * mm, "end": v(-39.3, -90.7) * mm, "construction": true});
            skLineSegment(sketch, "E238", {"start": v(-52.42, -64.42) * mm, "end": v(-39.3, -64.42) * mm, "construction": true});
            skArc(sketch, "E239.0.startCap", {"start": v(-34.3, -169.42) * mm, "mid": v(-39.3, -174.42) * mm, "end": v(-44.3, -169.42) * mm});
            skArc(sketch, "E239.0.endCap", {"start": v(-44.3, -143.16) * mm, "mid": v(-39.3, -138.16) * mm, "end": v(-34.3, -143.16) * mm});
            skLineSegment(sketch, "E239.0.left", {"start": v(-44.3, -169.42) * mm, "end": v(-44.3, -143.16) * mm});
            skLineSegment(sketch, "E239.0.right", {"start": v(-34.3, -169.42) * mm, "end": v(-34.3, -143.16) * mm});
            skArc(sketch, "E239.1.startCap", {"start": v(-34.3, -130.06) * mm, "mid": v(-39.3, -135.06) * mm, "end": v(-44.3, -130.06) * mm});
            skArc(sketch, "E239.1.endCap", {"start": v(-44.3, -103.8) * mm, "mid": v(-39.3, -98.8) * mm, "end": v(-34.3, -103.8) * mm});
            skLineSegment(sketch, "E239.1.left", {"start": v(-44.3, -130.06) * mm, "end": v(-44.3, -103.8) * mm});
            skLineSegment(sketch, "E239.1.right", {"start": v(-34.3, -130.06) * mm, "end": v(-34.3, -103.8) * mm});
            skArc(sketch, "E239.2.startCap", {"start": v(-44.3, -64.42) * mm, "mid": v(-39.3, -59.42) * mm, "end": v(-34.3, -64.42) * mm});
            skArc(sketch, "E239.2.endCap", {"start": v(-34.3, -90.7) * mm, "mid": v(-39.3, -95.7) * mm, "end": v(-44.3, -90.7) * mm});
            skLineSegment(sketch, "E239.2.left", {"start": v(-34.3, -64.42) * mm, "end": v(-34.3, -90.7) * mm});
            skLineSegment(sketch, "E239.2.right", {"start": v(-44.3, -64.42) * mm, "end": v(-44.3, -90.7) * mm});
            skLineSegment(sketch, "E240.1.0.0", {"start": v(-26.17, -103.8) * mm, "end": v(-26.17, -90.7) * mm, "construction": true});
            skArc(sketch, "E240.1.0.1", {"start": v(-21.17, -130.06) * mm, "mid": v(-26.17, -135.06) * mm, "end": v(-31.17, -130.06) * mm});
            skLineSegment(sketch, "E240.1.0.2", {"start": v(-21.17, -130.06) * mm, "end": v(-21.17, -103.8) * mm});
            skArc(sketch, "E240.1.0.3", {"start": v(-31.17, -143.16) * mm, "mid": v(-26.17, -138.16) * mm, "end": v(-21.17, -143.16) * mm});
            skLineSegment(sketch, "E240.1.0.4", {"start": v(-21.17, -169.42) * mm, "end": v(-21.17, -143.16) * mm});
            skPoint(sketch, "E240.1.0.5", {"position": v(-39.3, -69.1) * mm});
            skArc(sketch, "E240.1.0.6", {"start": v(-21.17, -169.42) * mm, "mid": v(-26.17, -174.42) * mm, "end": v(-31.17, -169.42) * mm});
            skLineSegment(sketch, "E240.1.0.7", {"start": v(-26.17, -169.42) * mm, "end": v(-26.17, -143.16) * mm, "construction": true});
            skLineSegment(sketch, "E240.1.0.8", {"start": v(-26.17, -143.16) * mm, "end": v(-26.17, -130.06) * mm, "construction": true});
            skLineSegment(sketch, "E240.1.0.9", {"start": v(-31.17, -169.42) * mm, "end": v(-31.17, -143.16) * mm});
            skLineSegment(sketch, "E240.1.0.10", {"start": v(-26.17, -130.06) * mm, "end": v(-26.17, -103.8) * mm, "construction": true});
            skArc(sketch, "E240.1.0.11", {"start": v(-31.17, -103.8) * mm, "mid": v(-26.17, -98.8) * mm, "end": v(-21.17, -103.8) * mm});
            skLineSegment(sketch, "E240.1.0.12", {"start": v(-31.17, -64.42) * mm, "end": v(-31.17, -90.7) * mm});
            skLineSegment(sketch, "E240.1.0.13", {"start": v(-31.17, -130.06) * mm, "end": v(-31.17, -103.8) * mm});
            skArc(sketch, "E240.1.0.14", {"start": v(-21.17, -90.7) * mm, "mid": v(-26.17, -95.7) * mm, "end": v(-31.17, -90.7) * mm});
            skLineSegment(sketch, "E240.1.0.15", {"start": v(-26.17, -64.42) * mm, "end": v(-26.17, -90.7) * mm, "construction": true});
            skLineSegment(sketch, "E240.1.0.16", {"start": v(-21.17, -64.42) * mm, "end": v(-21.17, -90.7) * mm});
            skArc(sketch, "E240.1.0.17", {"start": v(-31.17, -64.42) * mm, "mid": v(-26.17, -59.42) * mm, "end": v(-21.17, -64.42) * mm});
            skLineSegment(sketch, "E240.2.0.0", {"start": v(-13.05, -103.8) * mm, "end": v(-13.05, -90.7) * mm, "construction": true});
            skArc(sketch, "E240.2.0.1", {"start": v(-8.05, -130.06) * mm, "mid": v(-13.05, -135.06) * mm, "end": v(-18.05, -130.06) * mm});
            skLineSegment(sketch, "E240.2.0.2", {"start": v(-8.05, -130.06) * mm, "end": v(-8.05, -103.8) * mm});
            skArc(sketch, "E240.2.0.3", {"start": v(-18.05, -143.16) * mm, "mid": v(-13.05, -138.16) * mm, "end": v(-8.05, -143.16) * mm});
            skLineSegment(sketch, "E240.2.0.4", {"start": v(-8.05, -169.42) * mm, "end": v(-8.05, -143.16) * mm});
            skPoint(sketch, "E240.2.0.5", {"position": v(-26.17, -69.1) * mm});
            skArc(sketch, "E240.2.0.6", {"start": v(-8.05, -169.42) * mm, "mid": v(-13.05, -174.42) * mm, "end": v(-18.05, -169.42) * mm});
            skLineSegment(sketch, "E240.2.0.7", {"start": v(-13.05, -169.42) * mm, "end": v(-13.05, -143.16) * mm, "construction": true});
            skLineSegment(sketch, "E240.2.0.8", {"start": v(-13.05, -143.16) * mm, "end": v(-13.05, -130.06) * mm, "construction": true});
            skLineSegment(sketch, "E240.2.0.9", {"start": v(-18.05, -169.42) * mm, "end": v(-18.05, -143.16) * mm});
            skLineSegment(sketch, "E240.2.0.10", {"start": v(-13.05, -130.06) * mm, "end": v(-13.05, -103.8) * mm, "construction": true});
            skArc(sketch, "E240.2.0.11", {"start": v(-18.05, -103.8) * mm, "mid": v(-13.05, -98.8) * mm, "end": v(-8.05, -103.8) * mm});
            skLineSegment(sketch, "E240.2.0.12", {"start": v(-18.05, -64.42) * mm, "end": v(-18.05, -90.7) * mm});
            skLineSegment(sketch, "E240.2.0.13", {"start": v(-18.05, -130.06) * mm, "end": v(-18.05, -103.8) * mm});
            skArc(sketch, "E240.2.0.14", {"start": v(-8.05, -90.7) * mm, "mid": v(-13.05, -95.7) * mm, "end": v(-18.05, -90.7) * mm});
            skLineSegment(sketch, "E240.2.0.15", {"start": v(-13.05, -64.42) * mm, "end": v(-13.05, -90.7) * mm, "construction": true});
            skLineSegment(sketch, "E240.2.0.16", {"start": v(-8.05, -64.42) * mm, "end": v(-8.05, -90.7) * mm});
            skArc(sketch, "E240.2.0.17", {"start": v(-18.05, -64.42) * mm, "mid": v(-13.05, -59.42) * mm, "end": v(-8.05, -64.42) * mm});
            skLineSegment(sketch, "E240.3.0.0", {"start": v(0.08, -103.8) * mm, "end": v(0.08, -90.7) * mm, "construction": true});
            skArc(sketch, "E240.3.0.1", {"start": v(5.08, -130.06) * mm, "mid": v(0.08, -135.06) * mm, "end": v(-4.92, -130.06) * mm});
            skLineSegment(sketch, "E240.3.0.2", {"start": v(5.08, -130.06) * mm, "end": v(5.08, -103.8) * mm});
            skArc(sketch, "E240.3.0.3", {"start": v(-4.92, -143.16) * mm, "mid": v(0.08, -138.16) * mm, "end": v(5.08, -143.16) * mm});
            skLineSegment(sketch, "E240.3.0.4", {"start": v(5.08, -169.42) * mm, "end": v(5.08, -143.16) * mm});
            skPoint(sketch, "E240.3.0.5", {"position": v(-13.05, -69.1) * mm});
            skArc(sketch, "E240.3.0.6", {"start": v(5.08, -169.42) * mm, "mid": v(0.08, -174.42) * mm, "end": v(-4.92, -169.42) * mm});
            skLineSegment(sketch, "E240.3.0.7", {"start": v(0.08, -169.42) * mm, "end": v(0.08, -143.16) * mm, "construction": true});
            skLineSegment(sketch, "E240.3.0.8", {"start": v(0.08, -143.16) * mm, "end": v(0.08, -130.06) * mm, "construction": true});
            skLineSegment(sketch, "E240.3.0.9", {"start": v(-4.92, -169.42) * mm, "end": v(-4.92, -143.16) * mm});
            skLineSegment(sketch, "E240.3.0.10", {"start": v(0.08, -130.06) * mm, "end": v(0.08, -103.8) * mm, "construction": true});
            skArc(sketch, "E240.3.0.11", {"start": v(-4.92, -103.8) * mm, "mid": v(0.08, -98.8) * mm, "end": v(5.08, -103.8) * mm});
            skLineSegment(sketch, "E240.3.0.12", {"start": v(-4.92, -64.42) * mm, "end": v(-4.92, -90.7) * mm});
            skLineSegment(sketch, "E240.3.0.13", {"start": v(-4.92, -130.06) * mm, "end": v(-4.92, -103.8) * mm});
            skArc(sketch, "E240.3.0.14", {"start": v(5.08, -90.7) * mm, "mid": v(0.08, -95.7) * mm, "end": v(-4.92, -90.7) * mm});
            skLineSegment(sketch, "E240.3.0.15", {"start": v(0.08, -64.42) * mm, "end": v(0.08, -90.7) * mm, "construction": true});
            skLineSegment(sketch, "E240.3.0.16", {"start": v(5.08, -64.42) * mm, "end": v(5.08, -90.7) * mm});
            skArc(sketch, "E240.3.0.17", {"start": v(-4.92, -64.42) * mm, "mid": v(0.08, -59.42) * mm, "end": v(5.08, -64.42) * mm});
            skLineSegment(sketch, "E240.4.0.0", {"start": v(13.2, -103.8) * mm, "end": v(13.2, -90.7) * mm, "construction": true});
            skArc(sketch, "E240.4.0.1", {"start": v(18.2, -130.06) * mm, "mid": v(13.2, -135.06) * mm, "end": v(8.2, -130.06) * mm});
            skLineSegment(sketch, "E240.4.0.2", {"start": v(18.2, -130.06) * mm, "end": v(18.2, -103.8) * mm});
            skArc(sketch, "E240.4.0.3", {"start": v(8.2, -143.16) * mm, "mid": v(13.2, -138.16) * mm, "end": v(18.2, -143.16) * mm});
            skLineSegment(sketch, "E240.4.0.4", {"start": v(18.2, -169.42) * mm, "end": v(18.2, -143.16) * mm});
            skPoint(sketch, "E240.4.0.5", {"position": v(0.08, -69.1) * mm});
            skArc(sketch, "E240.4.0.6", {"start": v(18.2, -169.42) * mm, "mid": v(13.2, -174.42) * mm, "end": v(8.2, -169.42) * mm});
            skLineSegment(sketch, "E240.4.0.7", {"start": v(13.2, -169.42) * mm, "end": v(13.2, -143.16) * mm, "construction": true});
            skLineSegment(sketch, "E240.4.0.8", {"start": v(13.2, -143.16) * mm, "end": v(13.2, -130.06) * mm, "construction": true});
            skLineSegment(sketch, "E240.4.0.9", {"start": v(8.2, -169.42) * mm, "end": v(8.2, -143.16) * mm});
            skLineSegment(sketch, "E240.4.0.10", {"start": v(13.2, -130.06) * mm, "end": v(13.2, -103.8) * mm, "construction": true});
            skArc(sketch, "E240.4.0.11", {"start": v(8.2, -103.8) * mm, "mid": v(13.2, -98.8) * mm, "end": v(18.2, -103.8) * mm});
            skLineSegment(sketch, "E240.4.0.12", {"start": v(8.2, -64.42) * mm, "end": v(8.2, -90.7) * mm});
            skLineSegment(sketch, "E240.4.0.13", {"start": v(8.2, -130.06) * mm, "end": v(8.2, -103.8) * mm});
            skArc(sketch, "E240.4.0.14", {"start": v(18.2, -90.7) * mm, "mid": v(13.2, -95.7) * mm, "end": v(8.2, -90.7) * mm});
            skLineSegment(sketch, "E240.4.0.15", {"start": v(13.2, -64.42) * mm, "end": v(13.2, -90.7) * mm, "construction": true});
            skLineSegment(sketch, "E240.4.0.16", {"start": v(18.2, -64.42) * mm, "end": v(18.2, -90.7) * mm});
            skArc(sketch, "E240.4.0.17", {"start": v(8.2, -64.42) * mm, "mid": v(13.2, -59.42) * mm, "end": v(18.2, -64.42) * mm});
            skLineSegment(sketch, "E240.5.0.0", {"start": v(26.33, -103.8) * mm, "end": v(26.33, -90.7) * mm, "construction": true});
            skArc(sketch, "E240.5.0.1", {"start": v(31.33, -130.06) * mm, "mid": v(26.33, -135.06) * mm, "end": v(21.33, -130.06) * mm});
            skLineSegment(sketch, "E240.5.0.2", {"start": v(31.33, -130.06) * mm, "end": v(31.33, -103.8) * mm});
            skArc(sketch, "E240.5.0.3", {"start": v(21.33, -143.16) * mm, "mid": v(26.33, -138.16) * mm, "end": v(31.33, -143.16) * mm});
            skLineSegment(sketch, "E240.5.0.4", {"start": v(31.33, -169.42) * mm, "end": v(31.33, -143.16) * mm});
            skPoint(sketch, "E240.5.0.5", {"position": v(13.2, -69.1) * mm});
            skArc(sketch, "E240.5.0.6", {"start": v(31.33, -169.42) * mm, "mid": v(26.33, -174.42) * mm, "end": v(21.33, -169.42) * mm});
            skLineSegment(sketch, "E240.5.0.7", {"start": v(26.33, -169.42) * mm, "end": v(26.33, -143.16) * mm, "construction": true});
            skLineSegment(sketch, "E240.5.0.8", {"start": v(26.33, -143.16) * mm, "end": v(26.33, -130.06) * mm, "construction": true});
            skLineSegment(sketch, "E240.5.0.9", {"start": v(21.33, -169.42) * mm, "end": v(21.33, -143.16) * mm});
            skLineSegment(sketch, "E240.5.0.10", {"start": v(26.33, -130.06) * mm, "end": v(26.33, -103.8) * mm, "construction": true});
            skArc(sketch, "E240.5.0.11", {"start": v(21.33, -103.8) * mm, "mid": v(26.33, -98.8) * mm, "end": v(31.33, -103.8) * mm});
            skLineSegment(sketch, "E240.5.0.12", {"start": v(21.33, -64.42) * mm, "end": v(21.33, -90.7) * mm});
            skLineSegment(sketch, "E240.5.0.13", {"start": v(21.33, -130.06) * mm, "end": v(21.33, -103.8) * mm});
            skArc(sketch, "E240.5.0.14", {"start": v(31.33, -90.7) * mm, "mid": v(26.33, -95.7) * mm, "end": v(21.33, -90.7) * mm});
            skLineSegment(sketch, "E240.5.0.15", {"start": v(26.33, -64.42) * mm, "end": v(26.33, -90.7) * mm, "construction": true});
            skLineSegment(sketch, "E240.5.0.16", {"start": v(31.33, -64.42) * mm, "end": v(31.33, -90.7) * mm});
            skArc(sketch, "E240.5.0.17", {"start": v(21.33, -64.42) * mm, "mid": v(26.33, -59.42) * mm, "end": v(31.33, -64.42) * mm});
            skLineSegment(sketch, "E240.6.0.0", {"start": v(39.45, -103.8) * mm, "end": v(39.45, -90.7) * mm, "construction": true});
            skArc(sketch, "E240.6.0.1", {"start": v(44.45, -130.06) * mm, "mid": v(39.45, -135.06) * mm, "end": v(34.45, -130.06) * mm});
            skLineSegment(sketch, "E240.6.0.2", {"start": v(44.45, -130.06) * mm, "end": v(44.45, -103.8) * mm});
            skArc(sketch, "E240.6.0.3", {"start": v(34.45, -143.16) * mm, "mid": v(39.45, -138.16) * mm, "end": v(44.45, -143.16) * mm});
            skLineSegment(sketch, "E240.6.0.4", {"start": v(44.45, -169.42) * mm, "end": v(44.45, -143.16) * mm});
            skPoint(sketch, "E240.6.0.5", {"position": v(26.33, -69.1) * mm});
            skArc(sketch, "E240.6.0.6", {"start": v(44.45, -169.42) * mm, "mid": v(39.45, -174.42) * mm, "end": v(34.45, -169.42) * mm});
            skLineSegment(sketch, "E240.6.0.7", {"start": v(39.45, -169.42) * mm, "end": v(39.45, -143.16) * mm, "construction": true});
            skLineSegment(sketch, "E240.6.0.8", {"start": v(39.45, -143.16) * mm, "end": v(39.45, -130.06) * mm, "construction": true});
            skLineSegment(sketch, "E240.6.0.9", {"start": v(34.45, -169.42) * mm, "end": v(34.45, -143.16) * mm});
            skLineSegment(sketch, "E240.6.0.10", {"start": v(39.45, -130.06) * mm, "end": v(39.45, -103.8) * mm, "construction": true});
            skArc(sketch, "E240.6.0.11", {"start": v(34.45, -103.8) * mm, "mid": v(39.45, -98.8) * mm, "end": v(44.45, -103.8) * mm});
            skLineSegment(sketch, "E240.6.0.12", {"start": v(34.45, -64.42) * mm, "end": v(34.45, -90.7) * mm});
            skLineSegment(sketch, "E240.6.0.13", {"start": v(34.45, -130.06) * mm, "end": v(34.45, -103.8) * mm});
            skArc(sketch, "E240.6.0.14", {"start": v(44.45, -90.7) * mm, "mid": v(39.45, -95.7) * mm, "end": v(34.45, -90.7) * mm});
            skLineSegment(sketch, "E240.6.0.15", {"start": v(39.45, -64.42) * mm, "end": v(39.45, -90.7) * mm, "construction": true});
            skLineSegment(sketch, "E240.6.0.16", {"start": v(44.45, -64.42) * mm, "end": v(44.45, -90.7) * mm});
            skArc(sketch, "E240.6.0.17", {"start": v(34.45, -64.42) * mm, "mid": v(39.45, -59.42) * mm, "end": v(44.45, -64.42) * mm});
            skLineSegment(sketch, "E240.direction1", {"start": v(-44.3, -169.42) * mm, "end": v(-31.17, -169.42) * mm, "construction": true});
            skLineSegment(sketch, "E241", {"start": v(73.08, -42.92) * mm, "end": v(51.58, -42.92) * mm, "construction": true});
            skCircle(sketch, "E242", {"center": v(51.58, -42.92) * mm, "radius": 2 * mm});
            skLineSegment(sketch, "E243", {"start": v(73.08, -190.92) * mm, "end": v(51.58, -190.92) * mm, "construction": true});
            skCircle(sketch, "E244", {"center": v(51.58, -190.92) * mm, "radius": 2 * mm});
            skLineSegment(sketch, "E245", {"start": v(-72.92, -42.92) * mm, "end": v(-51.42, -42.92) * mm, "construction": true});
            skCircle(sketch, "E246", {"center": v(-51.42, -42.92) * mm, "radius": 2 * mm});
            skLineSegment(sketch, "E247", {"start": v(-72.92, -190.92) * mm, "end": v(-51.42, -190.92) * mm, "construction": true});
            skCircle(sketch, "E248", {"center": v(-51.42, -190.92) * mm, "radius": 2 * mm});
            skSolve(sketch);
        }
        {
            var Q0;
            Q0=qSketchRegion(id+"F35",true);
            extrude(context, id + "F36", {"entities" : qUnion([Q0]), "operationType" : NewBodyOperationType.REMOVE, "oppositeDirection" : true, "depth" : 25 * mm});
        }
        {
            var Q0;
            Q0=qCreatedBy(id+"F25.planeOp",FACE);
            var sketch = newSketch(context, id + "F37", { "sketchPlane" : qUnion([Q0])});
            skLineSegment(sketch, "E249", {"start": v(-112.23, -42.59) * mm, "end": v(-112.23, -95.59) * mm, "construction": true});
            skCircle(sketch, "E250", {"center": v(-112.23, -95.59) * mm, "radius": 1.6 * mm});
            skCircle(sketch, "E251", {"center": v(-112.23, -42.59) * mm, "radius": 1.6 * mm});
            skLineSegment(sketch, "E252.bottom", {"start": v(-100.23, -37.59) * mm, "end": v(-124.23, -37.59) * mm});
            skLineSegment(sketch, "E252.top", {"start": v(-100.23, -100.59) * mm, "end": v(-124.23, -100.59) * mm});
            skLineSegment(sketch, "E252.left", {"start": v(-100.23, -37.59) * mm, "end": v(-100.23, -100.59) * mm});
            skLineSegment(sketch, "E252.right", {"start": v(-124.23, -37.59) * mm, "end": v(-124.23, -100.59) * mm});
            skLineSegment(sketch, "E253", {"start": v(-112.23, -95.59) * mm, "end": v(-112.23, -100.59) * mm, "construction": true});
            skLineSegment(sketch, "E254", {"start": v(-112.23, -42.59) * mm, "end": v(-112.23, -37.59) * mm, "construction": true});
            skLineSegment(sketch, "E255", {"start": v(-102.23, -100.59) * mm, "end": v(-102.23, -37.59) * mm, "construction": true});
            skLineSegment(sketch, "E256", {"start": v(-100.23, -50.59) * mm, "end": v(-103.33, -50.59) * mm});
            skLineSegment(sketch, "E257", {"start": v(-103.33, -50.59) * mm, "end": v(-103.33, -90.59) * mm});
            skLineSegment(sketch, "E258", {"start": v(-103.33, -90.59) * mm, "end": v(-100.23, -90.59) * mm});
            skLineSegment(sketch, "E259", {"start": v(-119.23, -37.59) * mm, "end": v(-124.23, -42.59) * mm});
            skLineSegment(sketch, "E260", {"start": v(-119.23, -100.59) * mm, "end": v(-124.23, -95.59) * mm});
            skLineSegment(sketch, "E261", {"start": v(-124.23, -50.59) * mm, "end": v(-118.73, -50.59) * mm, "construction": true});
            skLineSegment(sketch, "E262", {"start": v(-118.73, -50.59) * mm, "end": v(-108.73, -50.59) * mm, "construction": true});
            skArc(sketch, "E263.0.startCap", {"start": v(-118.73, -52.59) * mm, "mid": v(-120.73, -50.59) * mm, "end": v(-118.73, -48.59) * mm});
            skArc(sketch, "E263.0.endCap", {"start": v(-108.73, -48.59) * mm, "mid": v(-106.73, -50.59) * mm, "end": v(-108.73, -52.59) * mm});
            skLineSegment(sketch, "E263.0.left", {"start": v(-118.73, -48.59) * mm, "end": v(-108.73, -48.59) * mm});
            skLineSegment(sketch, "E263.0.right", {"start": v(-118.73, -52.59) * mm, "end": v(-108.73, -52.59) * mm});
            skLineSegment(sketch, "E264.0.1.0", {"start": v(-118.73, -58.09) * mm, "end": v(-108.73, -58.09) * mm});
            skArc(sketch, "E264.0.1.1", {"start": v(-108.73, -58.09) * mm, "mid": v(-106.73, -60.09) * mm, "end": v(-108.73, -62.09) * mm});
            skLineSegment(sketch, "E264.0.1.2", {"start": v(-118.73, -62.09) * mm, "end": v(-108.73, -62.09) * mm});
            skArc(sketch, "E264.0.1.3", {"start": v(-118.73, -62.09) * mm, "mid": v(-120.73, -60.09) * mm, "end": v(-118.73, -58.09) * mm});
            skLineSegment(sketch, "E264.0.2.0", {"start": v(-118.73, -67.59) * mm, "end": v(-108.73, -67.59) * mm});
            skArc(sketch, "E264.0.2.1", {"start": v(-108.73, -67.59) * mm, "mid": v(-106.73, -69.59) * mm, "end": v(-108.73, -71.59) * mm});
            skLineSegment(sketch, "E264.0.2.2", {"start": v(-118.73, -71.59) * mm, "end": v(-108.73, -71.59) * mm});
            skArc(sketch, "E264.0.2.3", {"start": v(-118.73, -71.59) * mm, "mid": v(-120.73, -69.59) * mm, "end": v(-118.73, -67.59) * mm});
            skLineSegment(sketch, "E264.0.3.0", {"start": v(-118.73, -77.09) * mm, "end": v(-108.73, -77.09) * mm});
            skArc(sketch, "E264.0.3.1", {"start": v(-108.73, -77.09) * mm, "mid": v(-106.73, -79.09) * mm, "end": v(-108.73, -81.09) * mm});
            skLineSegment(sketch, "E264.0.3.2", {"start": v(-118.73, -81.09) * mm, "end": v(-108.73, -81.09) * mm});
            skArc(sketch, "E264.0.3.3", {"start": v(-118.73, -81.09) * mm, "mid": v(-120.73, -79.09) * mm, "end": v(-118.73, -77.09) * mm});
            skLineSegment(sketch, "E264.0.4.0", {"start": v(-118.73, -86.59) * mm, "end": v(-108.73, -86.59) * mm});
            skArc(sketch, "E264.0.4.1", {"start": v(-108.73, -86.59) * mm, "mid": v(-106.73, -88.59) * mm, "end": v(-108.73, -90.59) * mm});
            skLineSegment(sketch, "E264.0.4.2", {"start": v(-118.73, -90.59) * mm, "end": v(-108.73, -90.59) * mm});
            skArc(sketch, "E264.0.4.3", {"start": v(-118.73, -90.59) * mm, "mid": v(-120.73, -88.59) * mm, "end": v(-118.73, -86.59) * mm});
            skLineSegment(sketch, "E264.direction1", {"start": v(-118.73, -48.59) * mm, "end": v(-93.73, -48.59) * mm, "construction": true});
            skLineSegment(sketch, "E264.direction2", {"start": v(-118.73, -48.59) * mm, "end": v(-118.73, -58.09) * mm, "construction": true});
            skLineSegment(sketch, "E265", {"start": v(-101.23, -90.59) * mm, "end": v(-100.23, -91.59) * mm});
            skLineSegment(sketch, "E266", {"start": v(-101.23, -50.59) * mm, "end": v(-100.23, -49.59) * mm});
            skSolve(sketch);
        }
        {
            var Q0;
            Q0=makeQuery(id+"F37.imprint","IMPRINT",FACE,{"disambiguationData":[TD([[makeQuery(id+"F37.imprint","IMPRINT",EDGE,{"derivedFrom":sQuery(id+"F37.wireOp",EDGE,"E250")}),-1.0]])]});
            extrude(context, id + "F38", {"entities" : qUnion([Q0]), "depth" : 3 * mm});
        }
        {
            var Q0;
            Q0=makeQuery(id+"F10.boolean.opBoolean","COPY",EDGE,{"derivedFrom":makeQuery(id+"F10.opExtrude","SWEPT_EDGE",EDGE,{"disambiguationData":[OSD([sQuery(id+"F9.wireOp",EDGE,"E45.top"),sQuery(id+"F9.wireOp",EDGE,"E45.left")])]})});
            var Q1;
            Q1=makeQuery(id+"F10.boolean.opBoolean","COPY",EDGE,{"derivedFrom":makeQuery(id+"F10.opExtrude","SWEPT_EDGE",EDGE,{"disambiguationData":[OSD([sQuery(id+"F9.wireOp",EDGE,"E43.top"),sQuery(id+"F9.wireOp",EDGE,"E43.left")])]})});
            var Q2;
            Q2=makeQuery(id+"F10.boolean.opBoolean","COPY",EDGE,{"derivedFrom":makeQuery(id+"F10.opExtrude","SWEPT_EDGE",EDGE,{"disambiguationData":[OSD([sQuery(id+"F9.wireOp",EDGE,"E43.bottom"),sQuery(id+"F9.wireOp",EDGE,"E43.left")])]})});
            var Q3;
            Q3=makeQuery(id+"F10.boolean.opBoolean","COPY",EDGE,{"derivedFrom":makeQuery(id+"F10.opExtrude","SWEPT_EDGE",EDGE,{"disambiguationData":[OSD([sQuery(id+"F9.wireOp",EDGE,"E45.bottom"),sQuery(id+"F9.wireOp",EDGE,"E45.left")])]})});
            chamfer(context, id + "F39", {"entities" : qUnion([Q0, Q1, Q2, Q3]), "width" : .5 * mm, "tangentPropagation" : true});
        }
    });
